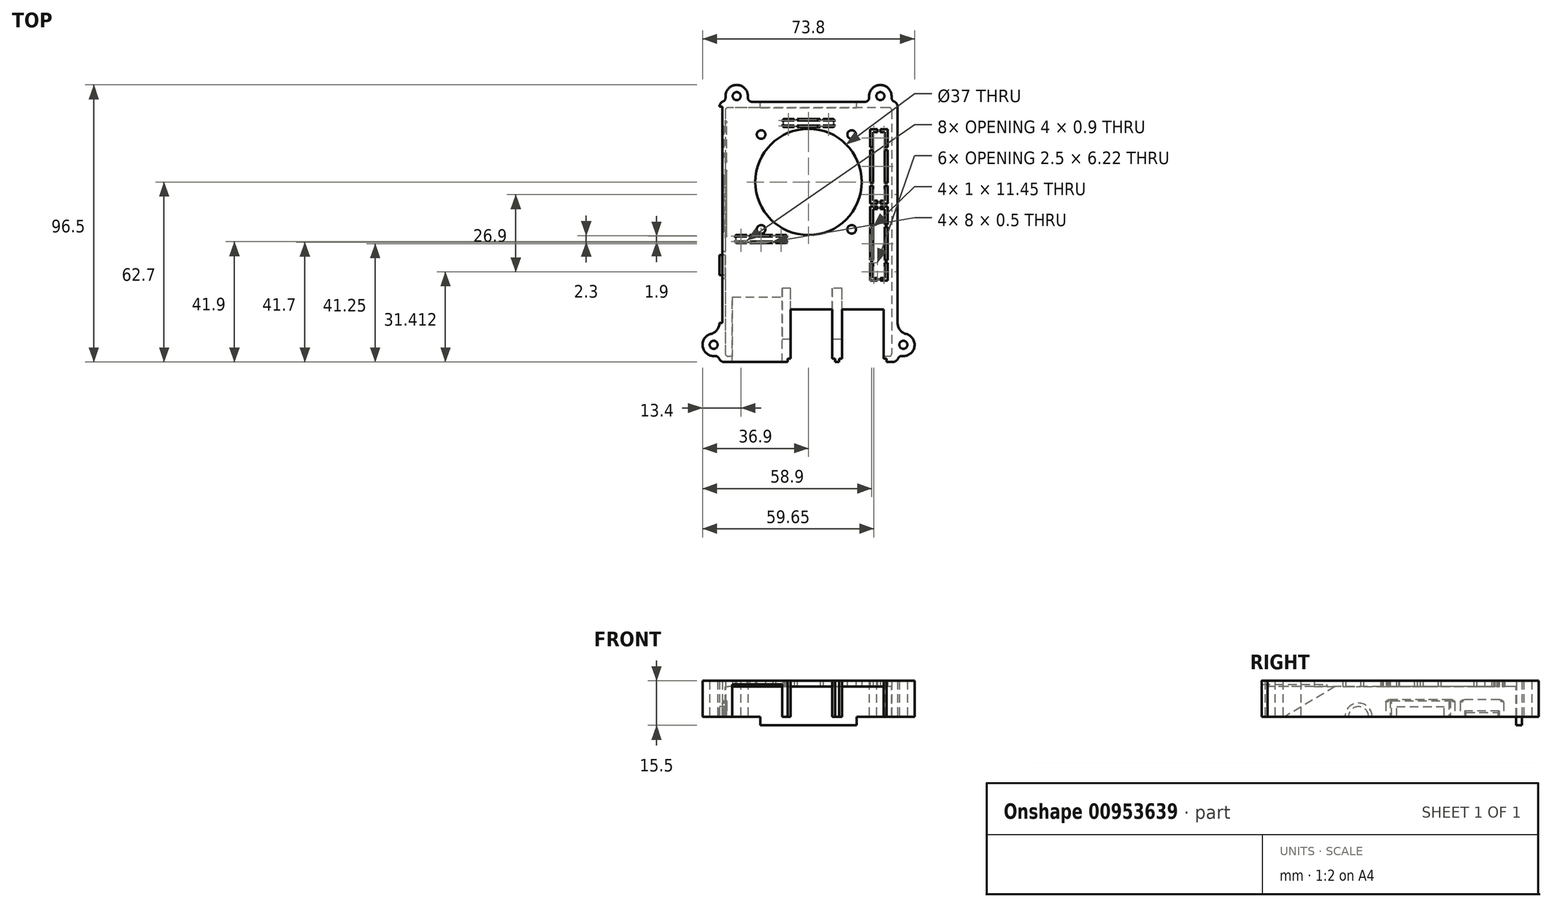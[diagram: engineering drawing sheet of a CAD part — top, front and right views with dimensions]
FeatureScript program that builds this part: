
annotation { "Feature Type Name" : "Feature", "Feature Type Description" : "" }
export const myFeature = defineFeature(function(context is Context, id is Id, definition is map)
    precondition{}
    {
        {
            var Q0;
            Q0=qCreatedBy(makeId("Top.planeOp"),FACE);
            var sketch = newSketch(context, id + "F0", { "sketchPlane" : qUnion([Q0])});
            skLineSegment(sketch, "E0.bottom", {"start": v(28, 43.3) * mm, "end": v(-28, 43.3) * mm});
            skLineSegment(sketch, "E0.top", {"start": v(28, -43.3) * mm, "end": v(-28, -43.3) * mm});
            skLineSegment(sketch, "E0.left", {"start": v(29, 42.3) * mm, "end": v(29, -42.3) * mm});
            skLineSegment(sketch, "E0.right", {"start": v(-29, 42.3) * mm, "end": v(-29, -42.3) * mm});
            skPoint(sketch, "E0.middle", {"position": v(0, 0) * mm});
            skLineSegment(sketch, "E1.0", {"start": v(31, 45.3) * mm, "end": v(31, -31.66) * mm});
            skLineSegment(sketch, "E1.1", {"start": v(31, 45.3) * mm, "end": v(30.38, 45.3) * mm});
            skLineSegment(sketch, "E1.2", {"start": v(-31, 45.3) * mm, "end": v(-31, -31.66) * mm});
            skLineSegment(sketch, "E1.3", {"start": v(31, -45.3) * mm, "end": v(-31, -45.3) * mm});
            skCircle(sketch, "E2", {"center": v(-25, 47.3) * mm, "radius": 1.4 * mm});
            skCircle(sketch, "E3", {"center": v(-33, -39.3) * mm, "radius": 1.4 * mm});
            skArc(sketch, "E4", {"start": v(-33.99, -35.53) * mm, "mid": v(-36.84, -39.98) * mm, "end": v(-32.64, -43.18) * mm});
            skArc(sketch, "E5", {"start": v(-21.12, 46.94) * mm, "mid": v(-25, 51.2) * mm, "end": v(-28.88, 46.94) * mm});
            skLineSegment(sketch, "E6.trimOffspring", {"start": v(-30.38, 45.3) * mm, "end": v(-31, 45.3) * mm});
            skLineSegment(sketch, "E7.trimOffspring", {"start": v(-31, -44.68) * mm, "end": v(-31, -45.3) * mm});
            skPoint(sketch, "E8.visualSharp", {"position": v(-31, -35.95) * mm});
            skArc(sketch, "E8.filletArc", {"start": v(-33.99, -35.53) * mm, "mid": v(-31.83, -34.1) * mm, "end": v(-31, -31.66) * mm});
            skPoint(sketch, "E9.visualSharp", {"position": v(-31, -42.65) * mm});
            skArc(sketch, "E9.filletArc", {"start": v(-31, -44.68) * mm, "mid": v(-31.49, -43.57) * mm, "end": v(-32.64, -43.18) * mm});
            skPoint(sketch, "E10.visualSharp", {"position": v(-28.35, 45.3) * mm});
            skArc(sketch, "E10.filletArc", {"start": v(-30.38, 45.3) * mm, "mid": v(-29.27, 45.79) * mm, "end": v(-28.88, 46.94) * mm});
            skPoint(sketch, "E11.visualSharp", {"position": v(-21.65, 45.3) * mm});
            skArc(sketch, "E11.filletArc", {"start": v(-21.12, 46.94) * mm, "mid": v(-20.73, 45.79) * mm, "end": v(-19.62, 45.3) * mm});
            skArc(sketch, "E12.MirrorCS", {"start": v(21.12, 46.94) * mm, "mid": v(20.73, 45.79) * mm, "end": v(19.62, 45.3) * mm});
            skCircle(sketch, "E13.MirrorC", {"center": v(25, 47.3) * mm, "radius": 1.4 * mm});
            skArc(sketch, "E14.MirrorCS", {"start": v(21.12, 46.94) * mm, "mid": v(25, 51.2) * mm, "end": v(28.88, 46.94) * mm});
            skArc(sketch, "E15.MirrorCS", {"start": v(30.38, 45.3) * mm, "mid": v(29.27, 45.79) * mm, "end": v(28.88, 46.94) * mm});
            skLineSegment(sketch, "E16.trimOffspring", {"start": v(19.62, 45.3) * mm, "end": v(-19.62, 45.3) * mm});
            skArc(sketch, "E17.MirrorCS", {"start": v(31, -44.68) * mm, "mid": v(31.49, -43.57) * mm, "end": v(32.64, -43.18) * mm});
            skCircle(sketch, "E18.MirrorC", {"center": v(33, -39.3) * mm, "radius": 1.4 * mm});
            skArc(sketch, "E19.MirrorCS", {"start": v(33.99, -35.53) * mm, "mid": v(36.84, -39.98) * mm, "end": v(32.64, -43.18) * mm});
            skArc(sketch, "E20.MirrorCS", {"start": v(33.99, -35.53) * mm, "mid": v(31.83, -34.1) * mm, "end": v(31, -31.66) * mm});
            skLineSegment(sketch, "E21.trimOffspring", {"start": v(31, -44.68) * mm, "end": v(31, -45.3) * mm});
            skPoint(sketch, "E22.visualSharp", {"position": v(-29, 43.3) * mm});
            skArc(sketch, "E22.filletArc", {"start": v(-28, 43.3) * mm, "mid": v(-28.7, 43) * mm, "end": v(-29, 42.3) * mm});
            skPoint(sketch, "E23.visualSharp", {"position": v(29, 43.3) * mm});
            skArc(sketch, "E23.filletArc", {"start": v(29, 42.3) * mm, "mid": v(28.7, 43) * mm, "end": v(28, 43.3) * mm});
            skPoint(sketch, "E24.visualSharp", {"position": v(-29, -43.3) * mm});
            skArc(sketch, "E24.filletArc", {"start": v(-29, -42.3) * mm, "mid": v(-28.7, -43) * mm, "end": v(-28, -43.3) * mm});
            skPoint(sketch, "E25.visualSharp", {"position": v(29, -43.3) * mm});
            skArc(sketch, "E25.filletArc", {"start": v(28, -43.3) * mm, "mid": v(28.7, -43) * mm, "end": v(29, -42.3) * mm});
            skLineSegment(sketch, "E26", {"start": v(-37.54, 31.4) * mm, "end": v(37.46, 31.4) * mm, "construction": true});
            skLineSegment(sketch, "E27", {"start": v(-37.54, 9.95) * mm, "end": v(37.46, 9.95) * mm, "construction": true});
            skLineSegment(sketch, "E28", {"start": v(-37.54, -11.55) * mm, "end": v(37.46, -11.55) * mm, "construction": true});
            skSolve(sketch);
        }
        {
            var Q0;
            Q0=makeQuery(id+"F0.imprint","IMPRINT",FACE,{"disambiguationData":[TD([[makeQuery(id+"F0.imprint","IMPRINT",EDGE,{"derivedFrom":sQuery(id+"F0.wireOp",EDGE,"E0.bottom")}),1.0]])]});
            var Q1;
            Q1=makeQuery(id+"F0.imprint","IMPRINT",FACE,{"disambiguationData":[TD([[makeQuery(id+"F0.imprint","IMPRINT",EDGE,{"derivedFrom":sQuery(id+"F0.wireOp",EDGE,"E0.bottom")}),-1.0]])]});
            var Q2;
            Q2=makeQuery(id+"F0.imprint","IMPRINT",FACE,{"disambiguationData":[TD([[makeQuery(id+"F0.imprint","IMPRINT",EDGE,{"derivedFrom":sQuery(id+"F0.wireOp",EDGE,"7KksbeZt-SgtM-qwzp-tZSZ-AhoeQB65ukFO")}),-1.0]])]});
            var Q3;
            Q3=makeQuery(id+"F0.imprint","IMPRINT",FACE,{"disambiguationData":[TD([[makeQuery(id+"F0.imprint","IMPRINT",EDGE,{"derivedFrom":sQuery(id+"F0.wireOp",EDGE,"7KksbeZt-SgtM-qwzp-tZSZ-AhoeQB65ukFO")}),1.0]])]});
            var Q4;
            Q4=makeQuery(id+"F0.imprint","IMPRINT",FACE,{"disambiguationData":[TD([[makeQuery(id+"F0.imprint","IMPRINT",EDGE,{"derivedFrom":sQuery(id+"F0.wireOp",EDGE,"5cbfba80-aa27-4a75-af92-75ae06634ded2.MirrorC")}),-1.0]])]});
            var Q5;
            Q5=makeQuery(id+"F0.imprint","IMPRINT",FACE,{"disambiguationData":[TD([[makeQuery(id+"F0.imprint","IMPRINT",EDGE,{"derivedFrom":sQuery(id+"F0.wireOp",EDGE,"5cbfba80-aa27-4a75-af92-75ae06634ded3.MirrorC")}),-1.0]])]});
            var Q6;
            Q6=makeQuery(id+"F0.imprint","IMPRINT",FACE,{"disambiguationData":[TD([[makeQuery(id+"F0.imprint","IMPRINT",EDGE,{"derivedFrom":sQuery(id+"F0.wireOp",EDGE,"8kVExDtM-LJhc-sOQH-PAKS-U9v5TH0pJNTE")}),-1.0]])]});
            var Q7;
            Q7=makeQuery(id+"F0.imprint","IMPRINT",FACE,{"disambiguationData":[TD([[makeQuery(id+"F0.imprint","IMPRINT",EDGE,{"derivedFrom":sQuery(id+"F0.wireOp",EDGE,"8kVExDtM-LJhc-sOQH-PAKS-U9v5TH0pJNTE")}),1.0]])]});
            var Q8;
            Q8=makeQuery(id+"F0.imprint","IMPRINT",FACE,{"disambiguationData":[TD([[makeQuery(id+"F0.imprint","IMPRINT",EDGE,{"derivedFrom":sQuery(id+"F0.wireOp",EDGE,"5cbfba80-aa27-4a75-af92-75ae06634ded0.MirrorC")}),-1.0]])]});
            var Q9;
            Q9=makeQuery(id+"F0.imprint","IMPRINT",FACE,{"disambiguationData":[TD([[makeQuery(id+"F0.imprint","IMPRINT",EDGE,{"derivedFrom":sQuery(id+"F0.wireOp",EDGE,"5cbfba80-aa27-4a75-af92-75ae06634ded0.MirrorC")}),1.0]])]});
            var Q10;
            Q10=makeQuery(id+"F0.imprint","IMPRINT",FACE,{"disambiguationData":[TD([[makeQuery(id+"F0.imprint","IMPRINT",EDGE,{"derivedFrom":sQuery(id+"F0.wireOp",EDGE,"dfaf72c4-a94b-42d6-8991-cf29f6b001300.MirrorC")}),-1.0]])]});
            var Q11;
            Q11=makeQuery(id+"F0.imprint","IMPRINT",FACE,{"disambiguationData":[TD([[makeQuery(id+"F0.imprint","IMPRINT",EDGE,{"derivedFrom":sQuery(id+"F0.wireOp",EDGE,"172ebd0b-a341-4e72-a369-0b862791728b.0")}),1.0]])]});
            var Q12;
            Q12=makeQuery(id+"F0.imprint","IMPRINT",FACE,{"disambiguationData":[TD([[makeQuery(id+"F0.imprint","IMPRINT",EDGE,{"derivedFrom":sQuery(id+"F0.wireOp",EDGE,"ufD7rTX0-MYzA-UZ21-AQa8-zzvgIyV9lOAw")}),1.0]])]});
            var Q13;
            Q13=makeQuery(id+"F0.imprint","IMPRINT",FACE,{"disambiguationData":[TD([[makeQuery(id+"F0.imprint","IMPRINT",EDGE,{"derivedFrom":sQuery(id+"F0.wireOp",EDGE,"5cbfba80-aa27-4a75-af92-75ae06634ded1.MirrorC")}),-1.0]])]});
            var Q14;
            Q14=makeQuery(id+"F0.imprint","IMPRINT",FACE,{"disambiguationData":[TD([[makeQuery(id+"F0.imprint","IMPRINT",EDGE,{"derivedFrom":sQuery(id+"F0.wireOp",EDGE,"56ec82e7-5166-41e1-9a52-937cd590b01a0.MirrorC")}),-1.0]])]});
            var Q15;
            Q15=makeQuery(id+"F0.imprint","IMPRINT",FACE,{"disambiguationData":[TD([[makeQuery(id+"F0.imprint","IMPRINT",EDGE,{"derivedFrom":sQuery(id+"F0.wireOp",EDGE,"b029ced5-7113-40fa-8cfa-9b4cbc9cc729.0")}),1.0]])]});
            var Q16;
            Q16=makeQuery(id+"F0.imprint","IMPRINT",FACE,{"disambiguationData":[TD([[makeQuery(id+"F0.imprint","IMPRINT",EDGE,{"derivedFrom":sQuery(id+"F0.wireOp",EDGE,"Lkb11Qj8-9LyP-TiyD-kAvs-BMHExQBuDsE0")}),1.0]])]});
            extrude(context, id + "F1", {"entities" : qUnion([Q0, Q1, Q2, Q3, Q4, Q5, Q6, Q7, Q8, Q9, Q10, Q11, Q12, Q13, Q14, Q15, Q16]), "depth" : 2 * mm, "offsetDistance" : 25 * mm});
        }
        {
            var Q0;
            Q0=makeQuery(id+"F0.imprint","IMPRINT",FACE,{"disambiguationData":[TD([[makeQuery(id+"F0.imprint","IMPRINT",EDGE,{"derivedFrom":sQuery(id+"F0.wireOp",EDGE,"E0.bottom")}),-1.0]])]});
            extrude(context, id + "F2", {"entities" : qUnion([Q0]), "operationType" : NewBodyOperationType.ADD, "oppositeDirection" : true, "depth" : 10.5 * mm, "offsetDistance" : 25 * mm});
        }
        {
            var Q0;
            {var subQ0=sQuery(id+"F0.wireOp",EDGE,"E6.trimOffspring");var subQ1=sQuery(id+"F0.wireOp",EDGE,"E1.2");Q0=makeQuery(id+"F2.boolean.opBoolean","MERGE",EDGE,{"derivedFrom":[makeQuery(id+"F1.opExtrude","SWEPT_EDGE",EDGE,{"disambiguationData":[OSD([subQ1,subQ0])]}),makeQuery(id+"F2.opExtrude","SWEPT_EDGE",EDGE,{"disambiguationData":[OSD([subQ1,subQ0])]})]});}
            var Q1;
            {var subQ0=sQuery(id+"F0.wireOp",EDGE,"E1.1");var subQ1=sQuery(id+"F0.wireOp",EDGE,"E1.0");Q1=makeQuery(id+"F2.boolean.opBoolean","MERGE",EDGE,{"derivedFrom":[makeQuery(id+"F1.opExtrude","SWEPT_EDGE",EDGE,{"disambiguationData":[OSD([subQ1,subQ0])]}),makeQuery(id+"F2.opExtrude","SWEPT_EDGE",EDGE,{"disambiguationData":[OSD([subQ1,subQ0])]})]});}
            var Q2;
            {var subQ0=sQuery(id+"F0.wireOp",EDGE,"E7.trimOffspring");var subQ1=sQuery(id+"F0.wireOp",EDGE,"E1.3");Q2=makeQuery(id+"F2.boolean.opBoolean","MERGE",EDGE,{"derivedFrom":[makeQuery(id+"F1.opExtrude","SWEPT_EDGE",EDGE,{"disambiguationData":[OSD([subQ1,subQ0])]}),makeQuery(id+"F2.opExtrude","SWEPT_EDGE",EDGE,{"disambiguationData":[OSD([subQ1,subQ0])]})]});}
            var Q3;
            {var subQ0=sQuery(id+"F0.wireOp",EDGE,"E21.trimOffspring");var subQ1=sQuery(id+"F0.wireOp",EDGE,"E1.3");Q3=makeQuery(id+"F2.boolean.opBoolean","MERGE",EDGE,{"derivedFrom":[makeQuery(id+"F1.opExtrude","SWEPT_EDGE",EDGE,{"disambiguationData":[OSD([subQ1,subQ0])]}),makeQuery(id+"F2.opExtrude","SWEPT_EDGE",EDGE,{"disambiguationData":[OSD([subQ1,subQ0])]})]});}
            fillet(context, id + "F3", {"entities" : qUnion([Q0, Q1, Q2, Q3]), "radius" : 2 * mm, "tangentPropagation" : true, "allowEdgeOverflow" : false});
        }
        {
            var Q0;
            Q0=makeQuery(id+"F2.opExtrude","CAP_FACE",FACE,{"disambiguationData":[OSD([sQuery(id+"F0.wireOp",EDGE,"E0.bottom"),sQuery(id+"F0.wireOp",EDGE,"E0.top"),sQuery(id+"F0.wireOp",EDGE,"E0.left"),sQuery(id+"F0.wireOp",EDGE,"E0.right"),sQuery(id+"F0.wireOp",EDGE,"E1.0"),sQuery(id+"F0.wireOp",EDGE,"E1.1"),sQuery(id+"F0.wireOp",EDGE,"E1.2"),sQuery(id+"F0.wireOp",EDGE,"E1.3"),sQuery(id+"F0.wireOp",EDGE,"E2"),sQuery(id+"F0.wireOp",EDGE,"E3"),sQuery(id+"F0.wireOp",EDGE,"E4"),sQuery(id+"F0.wireOp",EDGE,"E5"),sQuery(id+"F0.wireOp",EDGE,"E6.trimOffspring"),sQuery(id+"F0.wireOp",EDGE,"E7.trimOffspring"),sQuery(id+"F0.wireOp",EDGE,"E8.filletArc"),sQuery(id+"F0.wireOp",EDGE,"E9.filletArc"),sQuery(id+"F0.wireOp",EDGE,"E10.filletArc"),sQuery(id+"F0.wireOp",EDGE,"E11.filletArc"),sQuery(id+"F0.wireOp",EDGE,"E12.MirrorCS"),sQuery(id+"F0.wireOp",EDGE,"E13.MirrorC"),sQuery(id+"F0.wireOp",EDGE,"E14.MirrorCS"),sQuery(id+"F0.wireOp",EDGE,"E15.MirrorCS"),sQuery(id+"F0.wireOp",EDGE,"E16.trimOffspring"),sQuery(id+"F0.wireOp",EDGE,"E17.MirrorCS"),sQuery(id+"F0.wireOp",EDGE,"E18.MirrorC"),sQuery(id+"F0.wireOp",EDGE,"E19.MirrorCS"),sQuery(id+"F0.wireOp",EDGE,"E20.MirrorCS"),sQuery(id+"F0.wireOp",EDGE,"E21.trimOffspring"),sQuery(id+"F0.wireOp",EDGE,"E22.filletArc"),sQuery(id+"F0.wireOp",EDGE,"E23.filletArc"),sQuery(id+"F0.wireOp",EDGE,"E24.filletArc"),sQuery(id+"F0.wireOp",EDGE,"E25.filletArc")])],"isStart":false});
            var sketch = newSketch(context, id + "F4", { "sketchPlane" : qUnion([Q0])});
            skLineSegment(sketch, "E29.left", {"start": v(-29, -23.9) * mm, "end": v(-29, -38.9) * mm});
            skLineSegment(sketch, "E29.right", {"start": v(-28.5, -24.4) * mm, "end": v(-28.5, -38.4) * mm});
            skLineSegment(sketch, "E30", {"start": v(-29, -23.9) * mm, "end": v(-28.5, -24.4) * mm});
            skLineSegment(sketch, "E31", {"start": v(-29, -38.9) * mm, "end": v(-28.5, -38.4) * mm});
            skLineSegment(sketch, "E32.left", {"start": v(-29, 2.05) * mm, "end": v(-29, -21.95) * mm});
            skLineSegment(sketch, "E32.right", {"start": v(-28.5, 1.55) * mm, "end": v(-28.5, -21.45) * mm});
            skLineSegment(sketch, "E33", {"start": v(-29, 2.05) * mm, "end": v(-28.5, 1.55) * mm});
            skLineSegment(sketch, "E34", {"start": v(-29, -21.95) * mm, "end": v(-28.5, -21.45) * mm});
            skSolve(sketch);
        }
        {
            var Q0;
            Q0=qSketchRegion(id+"F4",true);
            extrude(context, id + "F5", {"entities" : qUnion([Q0]), "operationType" : NewBodyOperationType.ADD, "oppositeDirection" : true, "depth" : 6 * mm, "offsetDistance" : 25 * mm});
        }
        {
            var Q0;
            Q0=makeQuery(id+"F5.opExtrude","CAP_EDGE",EDGE,{"disambiguationData":[OSD([sQuery(id+"F4.wireOp",EDGE,"E32.right")])],"isStart":false});
            var Q1;
            Q1=makeQuery(id+"F5.opExtrude","CAP_EDGE",EDGE,{"disambiguationData":[OSD([sQuery(id+"F4.wireOp",EDGE,"E29.right")])],"isStart":false});
            var Q2;
            Q2=makeQuery(id+"F5.opExtrude","CAP_EDGE",EDGE,{"disambiguationData":[OSD([sQuery(id+"F4.wireOp",EDGE,"E34")])],"isStart":false});
            var Q3;
            Q3=makeQuery(id+"F5.opExtrude","CAP_EDGE",EDGE,{"disambiguationData":[OSD([sQuery(id+"F4.wireOp",EDGE,"E33")])],"isStart":false});
            var Q4;
            Q4=makeQuery(id+"F5.opExtrude","CAP_EDGE",EDGE,{"disambiguationData":[OSD([sQuery(id+"F4.wireOp",EDGE,"E31")])],"isStart":false});
            var Q5;
            Q5=makeQuery(id+"F5.opExtrude","CAP_EDGE",EDGE,{"disambiguationData":[OSD([sQuery(id+"F4.wireOp",EDGE,"E30")])],"isStart":false});
            fillet(context, id + "F6", {"entities" : qUnion([Q0, Q1, Q2, Q3, Q4, Q5]), "radius" : 1 * mm, "tangentPropagation" : true, "allowEdgeOverflow" : false});
        }
        {
            var Q0;
            Q0=makeQuery(id+"F6.opFillet","BLEND_EDGE",EDGE,{"blendedFrom":[makeQuery(id+"F5.opExtrude","CAP_EDGE",EDGE,{"disambiguationData":[OSD([sQuery(id+"F4.wireOp",EDGE,"E32.right")])],"isStart":false}),makeQuery(id+"F5.opExtrude","CAP_EDGE",EDGE,{"disambiguationData":[OSD([sQuery(id+"F4.wireOp",EDGE,"E34")])],"isStart":false})],"blendedInto":[]});
            var Q1;
            Q1=makeQuery(id+"F6.opFillet","BLEND_EDGE",EDGE,{"blendedFrom":[makeQuery(id+"F5.opExtrude","CAP_EDGE",EDGE,{"disambiguationData":[OSD([sQuery(id+"F4.wireOp",EDGE,"E32.right")])],"isStart":false}),makeQuery(id+"F5.opExtrude","CAP_EDGE",EDGE,{"disambiguationData":[OSD([sQuery(id+"F4.wireOp",EDGE,"E33")])],"isStart":false})],"blendedInto":[]});
            var Q2;
            Q2=makeQuery(id+"F6.opFillet","BLEND_EDGE",EDGE,{"blendedFrom":[makeQuery(id+"F5.opExtrude","CAP_EDGE",EDGE,{"disambiguationData":[OSD([sQuery(id+"F4.wireOp",EDGE,"E29.right")])],"isStart":false}),makeQuery(id+"F5.opExtrude","CAP_EDGE",EDGE,{"disambiguationData":[OSD([sQuery(id+"F4.wireOp",EDGE,"E31")])],"isStart":false})],"blendedInto":[]});
            var Q3;
            Q3=makeQuery(id+"F5.opExtrude","SWEPT_EDGE",EDGE,{"disambiguationData":[OSD([sQuery(id+"F4.wireOp",EDGE,"E29.right"),sQuery(id+"F4.wireOp",EDGE,"E30")])]});
            fillet(context, id + "F7", {"entities" : qUnion([Q0, Q1, Q2, Q3]), "radius" : 0.5 * mm, "tangentPropagation" : true, "allowEdgeOverflow" : false});
        }
        {
            var Q0;
            Q0=qCreatedBy(makeId("Right.planeOp"),FACE);
            var sketch = newSketch(context, id + "F8", { "sketchPlane" : qUnion([Q0])});
            skLineSegment(sketch, "E35", {"start": v(31.4, -3.36) * mm, "end": v(31.4, 15) * mm, "construction": true});
            skLineSegment(sketch, "E36", {"start": v(9.95, -3.36) * mm, "end": v(9.95, 15) * mm, "construction": true});
            skLineSegment(sketch, "E37", {"start": v(-11.55, -3.36) * mm, "end": v(-11.55, 15) * mm, "construction": true});
            skSolve(sketch);
        }
        {
            var Q0;
            {var subQ0=sQuery(id+"F0.wireOp",EDGE,"E1.2");Q0=makeQuery(id+"F2.boolean.opBoolean","MERGE",FACE,{"derivedFrom":[makeQuery(id+"F1.opExtrude","SWEPT_FACE",FACE,{"disambiguationData":[OSD([subQ0])]}),makeQuery(id+"F2.opExtrude","SWEPT_FACE",FACE,{"disambiguationData":[OSD([subQ0])]})]});}
            var sketch = newSketch(context, id + "F9", { "sketchPlane" : qUnion([Q0])});
            skArc(sketch, "E38.MirrorCS", {"start": v(6.8, -10.5) * mm, "mid": v(11.55, -5.75) * mm, "end": v(16.3, -10.5) * mm});
            skArc(sketch, "E39.MirrorCS", {"start": v(8.05, -10.5) * mm, "mid": v(11.55, -7) * mm, "end": v(15.05, -10.5) * mm});
            skPoint(sketch, "E40.end.orphan", {"position": v(15.05, -10.5) * mm});
            skPoint(sketch, "E40.start.orphan", {"position": v(8.05, -10.5) * mm});
            skPoint(sketch, "E41.end.orphan", {"position": v(16.3, -10.5) * mm});
            skPoint(sketch, "E41.start.orphan", {"position": v(6.8, -10.5) * mm});
            skSolve(sketch);
        }
        {
            var Q0;
            {var subQ0=sQuery(id+"F9.wireOp",EDGE,"E39.MirrorCS");Q0=makeQuery(id+"F9.imprint","IMPRINT",FACE,{"disambiguationData":[TD([[makeQuery(id+"F9.imprint","IMPRINT",EDGE,{"derivedFrom":subQ0}),-1.0]])]});}
            var Q1;
            Q1=makeQuery(id+"F2.opExtrude","SWEPT_FACE",FACE,{"disambiguationData":[OSD([sQuery(id+"F0.wireOp",EDGE,"E0.right")])]});
            extrude(context, id + "F10", {"entities" : qUnion([Q0]), "operationType" : NewBodyOperationType.REMOVE, "endBound" : BoundingType.UP_TO_SURFACE, "oppositeDirection" : true, "depth" : 25 * mm, "endBoundEntityFace" : qUnion([Q1]), "offsetDistance" : 25 * mm});
        }
        {
            var Q0;
            {var subQ0=sQuery(id+"F9.wireOp",EDGE,"E38.MirrorCS");Q0=makeQuery(id+"F9.imprint","IMPRINT",FACE,{"disambiguationData":[TD([[makeQuery(id+"F9.imprint","IMPRINT",EDGE,{"derivedFrom":subQ0}),-1.0]])]});}
            extrude(context, id + "F11", {"entities" : qUnion([Q0]), "operationType" : NewBodyOperationType.REMOVE, "oppositeDirection" : true, "depth" : 1 * mm, "offsetDistance" : 25 * mm});
        }
        {
            var Q0;
            {var subQ5=sQuery(id+"F9.wireOp",EDGE,"E38.MirrorCS");Q0=makeQuery(id+"F9.imprint","IMPRINT",FACE,{"disambiguationData":[TD([[makeQuery(id+"F9.imprint","IMPRINT",EDGE,{"derivedFrom":subQ5}),1.0]])]});}
            var sketch = newSketch(context, id + "F12", { "sketchPlane" : qUnion([Q0])});
            skLineSegment(sketch, "E42.bottom", {"start": v(-20.45, -4.5) * mm, "end": v(0.55, -4.5) * mm});
            skLineSegment(sketch, "E42.top", {"start": v(-20.45, -10.5) * mm, "end": v(0.55, -10.5) * mm});
            skLineSegment(sketch, "E42.left", {"start": v(-20.45, -4.5) * mm, "end": v(-20.45, -10.5) * mm});
            skLineSegment(sketch, "E42.right", {"start": v(0.55, -4.5) * mm, "end": v(0.55, -10.5) * mm});
            skLineSegment(sketch, "E43.0", {"start": v(-18.2, -7) * mm, "end": v(-18.2, -10.5) * mm});
            skLineSegment(sketch, "E44.0", {"start": v(-1.7, -7) * mm, "end": v(-1.7, -10.5) * mm});
            skLineSegment(sketch, "E45.0", {"start": v(-18.2, -7) * mm, "end": v(-1.7, -7) * mm});
            skLineSegment(sketch, "E46.bottom", {"start": v(-37.4, -8.5) * mm, "end": v(-25.4, -8.5) * mm});
            skLineSegment(sketch, "E46.top", {"start": v(-37.4, -10.5) * mm, "end": v(-25.4, -10.5) * mm});
            skLineSegment(sketch, "E46.left", {"start": v(-37.4, -8.5) * mm, "end": v(-37.4, -10.5) * mm});
            skLineSegment(sketch, "E46.right", {"start": v(-25.4, -8.5) * mm, "end": v(-25.4, -10.5) * mm});
            skSolve(sketch);
        }
        {
            var Q0;
            Q0=makeQuery(id+"F12.imprint","IMPRINT",FACE,{"disambiguationData":[TD([[makeQuery(id+"F12.imprint","IMPRINT",EDGE,{"derivedFrom":sQuery(id+"F12.wireOp",EDGE,"E46.bottom")}),-1.0]])]});
            var Q1;
            {var subQ0=sQuery(id+"F12.wireOp",EDGE,"2f087f3d-fe2a-414c-9c26-de2792726961.0");Q1=makeQuery(id+"F12.imprint","IMPRINT",FACE,{"disambiguationData":[TD([[makeQuery(id+"F12.imprint","IMPRINT",EDGE,{"derivedFrom":subQ0}),1.0]])]});}
            var Q2;
            Q2=makeQuery(id+"F12.imprint","IMPRINT",FACE,{"disambiguationData":[TD([[makeQuery(id+"F12.imprint","IMPRINT",EDGE,{"derivedFrom":sQuery(id+"F12.wireOp",EDGE,"E42.bottom")}),-1.0]])]});
            var Q3;
            {var subQ0=sQuery(id+"F12.wireOp",EDGE,"E43.0");Q3=makeQuery(id+"F12.imprint","IMPRINT",FACE,{"disambiguationData":[TD([[makeQuery(id+"F12.imprint","IMPRINT",EDGE,{"derivedFrom":subQ0}),1.0]])]});}
            var Q4;
            Q4=makeQuery(id+"F5.opExtrude","SWEPT_FACE",FACE,{"disambiguationData":[OSD([sQuery(id+"F4.wireOp",EDGE,"E29.right")])]});
            extrude(context, id + "F13", {"entities" : qUnion([Q0, Q1, Q2, Q3]), "operationType" : NewBodyOperationType.REMOVE, "oppositeDirection" : true, "depth" : 1.5 * mm, "endBoundEntityFace" : qUnion([Q4]), "offsetDistance" : 25 * mm});
        }
        {
            var Q0;
            {var subQ0=sQuery(id+"F12.wireOp",EDGE,"E43.0");Q0=makeQuery(id+"F12.imprint","IMPRINT",FACE,{"disambiguationData":[TD([[makeQuery(id+"F12.imprint","IMPRINT",EDGE,{"derivedFrom":subQ0}),1.0]])]});}
            var Q1;
            Q1=makeQuery(id+"F5.opExtrude","SWEPT_FACE",FACE,{"disambiguationData":[OSD([sQuery(id+"F4.wireOp",EDGE,"E29.right")])]});
            extrude(context, id + "F14", {"entities" : qUnion([Q0]), "operationType" : NewBodyOperationType.REMOVE, "endBound" : BoundingType.UP_TO_SURFACE, "oppositeDirection" : true, "depth" : 25 * mm, "endBoundEntityFace" : qUnion([Q1]), "offsetDistance" : 25 * mm});
        }
        {
            var Q0;
            Q0=makeQuery(id+"F13.boolean.opBoolean","COPY",EDGE,{"derivedFrom":makeQuery(id+"F13.opExtrude","CAP_EDGE",EDGE,{"disambiguationData":[OSD([sQuery(id+"F12.wireOp",EDGE,"E42.left")])],"isStart":false})});
            var Q1;
            Q1=makeQuery(id+"F13.boolean.opBoolean","COPY",EDGE,{"derivedFrom":makeQuery(id+"F13.opExtrude","CAP_EDGE",EDGE,{"disambiguationData":[OSD([sQuery(id+"F12.wireOp",EDGE,"E42.bottom")])],"isStart":false})});
            var Q2;
            Q2=makeQuery(id+"F13.boolean.opBoolean","COPY",EDGE,{"derivedFrom":makeQuery(id+"F13.opExtrude","CAP_EDGE",EDGE,{"disambiguationData":[OSD([sQuery(id+"F12.wireOp",EDGE,"E42.right")])],"isStart":false})});
            var Q3;
            Q3=makeQuery(id+"F13.boolean.opBoolean","COPY",EDGE,{"derivedFrom":makeQuery(id+"F13.opExtrude","CAP_EDGE",EDGE,{"disambiguationData":[OSD([sQuery(id+"F12.wireOp",EDGE,"E46.right")])],"isStart":false})});
            var Q4;
            Q4=makeQuery(id+"F13.boolean.opBoolean","COPY",EDGE,{"derivedFrom":makeQuery(id+"F13.opExtrude","CAP_EDGE",EDGE,{"disambiguationData":[OSD([sQuery(id+"F12.wireOp",EDGE,"E46.bottom")])],"isStart":false})});
            var Q5;
            Q5=makeQuery(id+"F13.boolean.opBoolean","COPY",EDGE,{"derivedFrom":makeQuery(id+"F13.opExtrude","CAP_EDGE",EDGE,{"disambiguationData":[OSD([sQuery(id+"F12.wireOp",EDGE,"E46.left")])],"isStart":false})});
            chamfer(context, id + "F15", {"entities" : qUnion([Q0, Q1, Q2, Q3, Q4, Q5]), "width" : 0.5 * mm, "tangentPropagation" : true});
        }
        {
            var Q0;
            {var subQ4=sQuery(id+"F0.wireOp",EDGE,"E16.trimOffspring");var subQ7=sQuery(id+"F0.wireOp",EDGE,"E12.MirrorCS");Q0=makeQuery(id+"FgmCDMeV1RtUn8Z_1.boolean.opBoolean","SPLIT",FACE,{"disambiguationData":[TD([makeQuery(id+"F1.opExtrude","SWEPT_FACE",FACE,{"disambiguationData":[OSD([subQ7])]})])],"derivedFrom":makeQuery(id+"F2.boolean.opBoolean","MERGE",FACE,{"derivedFrom":[makeQuery(id+"F1.opExtrude","SWEPT_FACE",FACE,{"disambiguationData":[OSD([subQ4])]}),makeQuery(id+"F2.opExtrude","SWEPT_FACE",FACE,{"disambiguationData":[OSD([subQ4])]})]})});}
            var sketch = newSketch(context, id + "F16", { "sketchPlane" : qUnion([Q0])});
            skLineSegment(sketch, "E47.bottom", {"start": v(-16.8, -10.5) * mm, "end": v(16.8, -10.5) * mm});
            skLineSegment(sketch, "E47.top", {"start": v(-16.8, -13.5) * mm, "end": v(16.8, -13.5) * mm});
            skLineSegment(sketch, "E47.left", {"start": v(-16.8, -10.5) * mm, "end": v(-16.8, -13.5) * mm});
            skLineSegment(sketch, "E47.right", {"start": v(16.8, -10.5) * mm, "end": v(16.8, -13.5) * mm});
            skSolve(sketch);
        }
        {
            var Q0;
            Q0=makeQuery(id+"F16.imprint","IMPRINT",FACE,{"disambiguationData":[TD([[makeQuery(id+"F16.imprint","IMPRINT",EDGE,{"derivedFrom":sQuery(id+"F16.wireOp",EDGE,"E47.bottom")}),-1.0]])]});
            var Q1;
            Q1=makeQuery(id+"F2.opExtrude","SWEPT_FACE",FACE,{"disambiguationData":[OSD([sQuery(id+"F0.wireOp",EDGE,"E0.bottom")])]});
            extrude(context, id + "F17", {"entities" : qUnion([Q0]), "operationType" : NewBodyOperationType.ADD, "endBound" : BoundingType.UP_TO_SURFACE, "oppositeDirection" : true, "depth" : 2 * mm, "endBoundEntityFace" : qUnion([Q1]), "offsetDistance" : 25 * mm});
        }
        {
            var Q0;
            {var subQ0=sQuery(id+"F0.wireOp",EDGE,"E4");var subQ2=sQuery(id+"F0.wireOp",EDGE,"E0.left");var subQ4=sQuery(id+"F0.wireOp",EDGE,"E0.top");var subQ6=sQuery(id+"F0.wireOp",EDGE,"E1.1");var subQ7=sQuery(id+"F0.wireOp",EDGE,"E1.0");var subQ9=sQuery(id+"F0.wireOp",EDGE,"E0.bottom");var subQ11=sQuery(id+"F0.wireOp",EDGE,"E3");var subQ13=sQuery(id+"F0.wireOp",EDGE,"E20.MirrorCS");var subQ15=sQuery(id+"F0.wireOp",EDGE,"E19.MirrorCS");var subQ17=sQuery(id+"F0.wireOp",EDGE,"E1.3");var subQ19=sQuery(id+"F0.wireOp",EDGE,"E17.MirrorCS");var subQ25=sQuery(id+"F0.wireOp",EDGE,"E1.2");var subQ27=sQuery(id+"F0.wireOp",EDGE,"E16.trimOffspring");var subQ30=sQuery(id+"F0.wireOp",EDGE,"E18.MirrorC");var subQ33=sQuery(id+"F0.wireOp",EDGE,"E7.trimOffspring");var subQ35=sQuery(id+"F0.wireOp",EDGE,"E14.MirrorCS");var subQ41=sQuery(id+"F0.wireOp",EDGE,"E15.MirrorCS");var subQ43=makeQuery(id+"F1.opExtrude","SWEPT_FACE",FACE,{"disambiguationData":[OSD([subQ7])]});var subQ45=sQuery(id+"F0.wireOp",EDGE,"E9.filletArc");var subQ47=sQuery(id+"F0.wireOp",EDGE,"E25.filletArc");var subQ49=sQuery(id+"F0.wireOp",EDGE,"E8.filletArc");var subQ51=sQuery(id+"F0.wireOp",EDGE,"E24.filletArc");var subQ53=sQuery(id+"F0.wireOp",EDGE,"E0.right");var subQ55=sQuery(id+"F0.wireOp",EDGE,"E21.trimOffspring");var subQ57=sQuery(id+"F0.wireOp",EDGE,"E12.MirrorCS");var subQ62=sQuery(id+"F0.wireOp",EDGE,"E13.MirrorC");var subQ68=sQuery(id+"F0.wireOp",EDGE,"E23.filletArc");var subQ70=sQuery(id+"F0.wireOp",EDGE,"E22.filletArc");var subQ71=sQuery(id+"F0.wireOp",EDGE,"E11.filletArc");var subQ72=sQuery(id+"F0.wireOp",EDGE,"E10.filletArc");var subQ73=sQuery(id+"F0.wireOp",EDGE,"E5");var subQ74=sQuery(id+"F0.wireOp",EDGE,"E6.trimOffspring");var subQ75=sQuery(id+"F0.wireOp",EDGE,"E2");var subQ76=sQuery(id+"F4.wireOp",EDGE,"E29.right");var subQ77=sQuery(id+"F4.wireOp",EDGE,"E30");Q0=makeQuery(id+"FgmCDMeV1RtUn8Z_1.boolean.opBoolean","SPLIT",FACE,{"disambiguationData":[TD([subQ43])],"derivedFrom":makeQuery(id+"F14.boolean.opBoolean","SPLIT",FACE,{"disambiguationData":[TD([subQ43])],"derivedFrom":makeQuery(id+"F5.boolean.opBoolean","MERGE",FACE,{"derivedFrom":[makeQuery(id+"F2.opExtrude","CAP_FACE",FACE,{"disambiguationData":[OSD([subQ9,subQ4,subQ2,subQ53,subQ7,subQ6,subQ25,subQ17,subQ75,subQ11,subQ0,subQ73,subQ74,subQ33,subQ49,subQ45,subQ72,subQ71,subQ57,subQ62,subQ35,subQ41,subQ27,subQ19,subQ30,subQ15,subQ13,subQ55,subQ70,subQ68,subQ51,subQ47])],"isStart":false}),makeQuery(id+"F5.opExtrude","CAP_FACE",FACE,{"disambiguationData":[OSD([sQuery(id+"F4.wireOp",EDGE,"E29.left"),subQ76,subQ77,sQuery(id+"F4.wireOp",EDGE,"E31")])],"isStart":true}),makeQuery(id+"F5.opExtrude","CAP_FACE",FACE,{"disambiguationData":[OSD([sQuery(id+"F4.wireOp",EDGE,"E32.left"),sQuery(id+"F4.wireOp",EDGE,"E32.right"),sQuery(id+"F4.wireOp",EDGE,"E33"),sQuery(id+"F4.wireOp",EDGE,"E34")])],"isStart":true})]})})});}
            var sketch = newSketch(context, id + "F18", { "sketchPlane" : qUnion([Q0])});
            skLineSegment(sketch, "E48", {"start": v(-7.7, 63.26) * mm, "end": v(-7.7, 18.26) * mm, "construction": true});
            skLineSegment(sketch, "E49", {"start": v(9.95, 63.26) * mm, "end": v(9.95, 18.26) * mm, "construction": true});
            skLineSegment(sketch, "E50.bottom", {"start": v(-9.1, 43.3) * mm, "end": v(-6.3, 43.3) * mm});
            skLineSegment(sketch, "E50.top", {"start": v(-9.1, 16.3) * mm, "end": v(-6.3, 16.3) * mm});
            skLineSegment(sketch, "E50.left", {"start": v(-9.1, 43.3) * mm, "end": v(-9.1, 16.3) * mm});
            skLineSegment(sketch, "E50.right", {"start": v(-6.3, 43.3) * mm, "end": v(-6.3, 16.3) * mm});
            skLineSegment(sketch, "E51.bottom", {"start": v(8.2, 43.3) * mm, "end": v(11.7, 43.3) * mm});
            skLineSegment(sketch, "E51.top", {"start": v(8.2, 16.3) * mm, "end": v(11.7, 16.3) * mm});
            skLineSegment(sketch, "E51.left", {"start": v(8.2, 43.3) * mm, "end": v(8.2, 16.3) * mm});
            skLineSegment(sketch, "E51.right", {"start": v(11.7, 43.3) * mm, "end": v(11.7, 16.3) * mm});
            skSolve(sketch);
        }
        {
            var Q0;
            Q0=qSketchRegion(id+"F18",true);
            var Q1;
            Q1=makeQuery(id+"F1.opExtrude","CAP_FACE",FACE,{"disambiguationData":[OSD([sQuery(id+"F0.wireOp",EDGE,"E1.0"),sQuery(id+"F0.wireOp",EDGE,"E1.1"),sQuery(id+"F0.wireOp",EDGE,"E1.2"),sQuery(id+"F0.wireOp",EDGE,"E1.3"),sQuery(id+"F0.wireOp",EDGE,"E2"),sQuery(id+"F0.wireOp",EDGE,"E3"),sQuery(id+"F0.wireOp",EDGE,"E4"),sQuery(id+"F0.wireOp",EDGE,"E5"),sQuery(id+"F0.wireOp",EDGE,"E6.trimOffspring"),sQuery(id+"F0.wireOp",EDGE,"E7.trimOffspring"),sQuery(id+"F0.wireOp",EDGE,"E8.filletArc"),sQuery(id+"F0.wireOp",EDGE,"E9.filletArc"),sQuery(id+"F0.wireOp",EDGE,"E10.filletArc"),sQuery(id+"F0.wireOp",EDGE,"E11.filletArc"),sQuery(id+"F0.wireOp",EDGE,"E12.MirrorCS"),sQuery(id+"F0.wireOp",EDGE,"E13.MirrorC"),sQuery(id+"F0.wireOp",EDGE,"E14.MirrorCS"),sQuery(id+"F0.wireOp",EDGE,"E15.MirrorCS"),sQuery(id+"F0.wireOp",EDGE,"E16.trimOffspring"),sQuery(id+"F0.wireOp",EDGE,"E17.MirrorCS"),sQuery(id+"F0.wireOp",EDGE,"E18.MirrorC"),sQuery(id+"F0.wireOp",EDGE,"E19.MirrorCS"),sQuery(id+"F0.wireOp",EDGE,"E20.MirrorCS"),sQuery(id+"F0.wireOp",EDGE,"E21.trimOffspring")])],"isStart":true});
            extrude(context, id + "F19", {"entities" : qUnion([Q0]), "operationType" : NewBodyOperationType.ADD, "endBound" : BoundingType.UP_TO_SURFACE, "oppositeDirection" : true, "depth" : 0.5 * mm, "endBoundEntityFace" : qUnion([Q1]), "offsetDistance" : 25 * mm});
        }
        {
            var Q0;
            Q0=makeQuery(id+"F19.opExtrude","CAP_EDGE",EDGE,{"disambiguationData":[OSD([sQuery(id+"F18.wireOp",EDGE,"E50.top")])],"isStart":true});
            var Q1;
            Q1=makeQuery(id+"F19.opExtrude","CAP_EDGE",EDGE,{"disambiguationData":[OSD([sQuery(id+"F18.wireOp",EDGE,"E51.top")])],"isStart":true});
            chamfer(context, id + "F20", {"entities" : qUnion([Q0, Q1]), "chamferType" : ChamferType.TWO_OFFSETS, "width1" : 21 * mm, "oppositeDirection" : false, "width2" : 12.5 * mm, "tangentPropagation" : true});
        }
        {
            var Q0;
            Q0=qCreatedBy(makeId("Top.planeOp"),FACE);
            var sketch = newSketch(context, id + "F21", { "sketchPlane" : qUnion([Q0])});
            skLineSegment(sketch, "E52", {"start": v(-17.75, 15.2) * mm, "end": v(-17.75, -55.38) * mm, "construction": true});
            skLineSegment(sketch, "E53", {"start": v(0.95, 15.2) * mm, "end": v(0.95, -55.38) * mm, "construction": true});
            skLineSegment(sketch, "E54", {"start": v(18.95, 15.2) * mm, "end": v(18.95, -55.38) * mm, "construction": true});
            skSolve(sketch);
        }
        {
            var Q0;
            Q0=makeQuery(id+"F1.opExtrude","CAP_FACE",FACE,{"disambiguationData":[OSD([sQuery(id+"F0.wireOp",EDGE,"E1.0"),sQuery(id+"F0.wireOp",EDGE,"E1.1"),sQuery(id+"F0.wireOp",EDGE,"E1.2"),sQuery(id+"F0.wireOp",EDGE,"E1.3"),sQuery(id+"F0.wireOp",EDGE,"E2"),sQuery(id+"F0.wireOp",EDGE,"E3"),sQuery(id+"F0.wireOp",EDGE,"E4"),sQuery(id+"F0.wireOp",EDGE,"E5"),sQuery(id+"F0.wireOp",EDGE,"E6.trimOffspring"),sQuery(id+"F0.wireOp",EDGE,"E7.trimOffspring"),sQuery(id+"F0.wireOp",EDGE,"E8.filletArc"),sQuery(id+"F0.wireOp",EDGE,"E9.filletArc"),sQuery(id+"F0.wireOp",EDGE,"E10.filletArc"),sQuery(id+"F0.wireOp",EDGE,"E11.filletArc"),sQuery(id+"F0.wireOp",EDGE,"E12.MirrorCS"),sQuery(id+"F0.wireOp",EDGE,"E13.MirrorC"),sQuery(id+"F0.wireOp",EDGE,"E14.MirrorCS"),sQuery(id+"F0.wireOp",EDGE,"E15.MirrorCS"),sQuery(id+"F0.wireOp",EDGE,"E16.trimOffspring"),sQuery(id+"F0.wireOp",EDGE,"E17.MirrorCS"),sQuery(id+"F0.wireOp",EDGE,"E18.MirrorC"),sQuery(id+"F0.wireOp",EDGE,"E19.MirrorCS"),sQuery(id+"F0.wireOp",EDGE,"E20.MirrorCS"),sQuery(id+"F0.wireOp",EDGE,"E21.trimOffspring")])],"isStart":true});
            var sketch = newSketch(context, id + "F22", { "sketchPlane" : qUnion([Q0])});
            skLineSegment(sketch, "E55.bottom", {"start": v(-9.1, 45.3) * mm, "end": v(-26.5, 45.3) * mm});
            skLineSegment(sketch, "E55.top", {"start": v(-9.1, 22.6) * mm, "end": v(-26.5, 22.6) * mm});
            skLineSegment(sketch, "E55.left", {"start": v(-9.1, 45.3) * mm, "end": v(-9.1, 22.6) * mm});
            skLineSegment(sketch, "E55.right", {"start": v(-26.5, 45.3) * mm, "end": v(-26.5, 22.6) * mm});
            skLineSegment(sketch, "E56.top", {"start": v(8.2, 27) * mm, "end": v(-6.3, 27) * mm});
            skLineSegment(sketch, "E56.left", {"start": v(8.2, 44.1) * mm, "end": v(8.2, 27) * mm});
            skLineSegment(sketch, "E56.right", {"start": v(-6.3, 44.1) * mm, "end": v(-6.3, 27) * mm});
            skLineSegment(sketch, "E57", {"start": v(-7.3, 44.1) * mm, "end": v(-6.3, 44.1) * mm});
            skLineSegment(sketch, "E58", {"start": v(9.2, 45.3) * mm, "end": v(9.2, 44.1) * mm});
            skLineSegment(sketch, "E59", {"start": v(9.2, 44.1) * mm, "end": v(8.2, 44.1) * mm});
            skLineSegment(sketch, "E60", {"start": v(-7.3, 45.3) * mm, "end": v(9.2, 45.3) * mm});
            skLineSegment(sketch, "E61", {"start": v(-7.3, 44.1) * mm, "end": v(-7.3, 45.3) * mm});
            skLineSegment(sketch, "E62.bottom", {"start": v(10.7, 45.3) * mm, "end": v(27.2, 45.3) * mm});
            skLineSegment(sketch, "E62.top", {"start": v(11.7, 27) * mm, "end": v(26.2, 27) * mm});
            skLineSegment(sketch, "E62.left", {"start": v(11.7, 44.1) * mm, "end": v(11.7, 27) * mm});
            skLineSegment(sketch, "E62.right", {"start": v(26.2, 44.1) * mm, "end": v(26.2, 27) * mm});
            skLineSegment(sketch, "E63", {"start": v(10.7, 45.3) * mm, "end": v(10.7, 44.1) * mm});
            skLineSegment(sketch, "E64", {"start": v(10.7, 44.1) * mm, "end": v(11.7, 44.1) * mm});
            skLineSegment(sketch, "E65", {"start": v(27.2, 45.3) * mm, "end": v(27.2, 44.1) * mm});
            skLineSegment(sketch, "E66", {"start": v(27.2, 44.1) * mm, "end": v(26.2, 44.1) * mm});
            skSolve(sketch);
        }
        {
            var Q0;
            {var subQ0=sQuery(id+"F22.wireOp",EDGE,"E55.top");Q0=makeQuery(id+"F22.imprint","IMPRINT",FACE,{"disambiguationData":[TD([[makeQuery(id+"F22.imprint","IMPRINT",EDGE,{"derivedFrom":subQ0}),-1.0]])]});}
            var Q1;
            {var subQ0=sQuery(id+"F22.wireOp",EDGE,"E55.bottom");Q1=makeQuery(id+"F22.imprint","IMPRINT",FACE,{"disambiguationData":[TD([[makeQuery(id+"F22.imprint","IMPRINT",EDGE,{"derivedFrom":subQ0}),1.0]])]});}
            var Q2;
            {var subQ4=sQuery(id+"F0.wireOp",EDGE,"E25.filletArc");var subQ6=sQuery(id+"F0.wireOp",EDGE,"E24.filletArc");var subQ8=sQuery(id+"F0.wireOp",EDGE,"E23.filletArc");var subQ10=sQuery(id+"F0.wireOp",EDGE,"E20.MirrorCS");var subQ12=sQuery(id+"F0.wireOp",EDGE,"E17.MirrorCS");var subQ14=sQuery(id+"F0.wireOp",EDGE,"E16.trimOffspring");var subQ16=sQuery(id+"F0.wireOp",EDGE,"E15.MirrorCS");var subQ18=sQuery(id+"F0.wireOp",EDGE,"E13.MirrorC");var subQ20=sQuery(id+"F0.wireOp",EDGE,"E12.MirrorCS");var subQ22=sQuery(id+"F0.wireOp",EDGE,"E9.filletArc");var subQ24=sQuery(id+"F0.wireOp",EDGE,"E19.MirrorCS");var subQ26=sQuery(id+"F0.wireOp",EDGE,"E8.filletArc");var subQ28=sQuery(id+"F0.wireOp",EDGE,"E18.MirrorC");var subQ30=sQuery(id+"F0.wireOp",EDGE,"E4");var subQ32=sQuery(id+"F0.wireOp",EDGE,"E1.1");var subQ33=sQuery(id+"F0.wireOp",EDGE,"E1.0");var subQ35=sQuery(id+"F0.wireOp",EDGE,"E14.MirrorCS");var subQ37=sQuery(id+"F0.wireOp",EDGE,"E3");var subQ40=sQuery(id+"F0.wireOp",EDGE,"E1.3");var subQ42=sQuery(id+"F0.wireOp",EDGE,"E1.2");var subQ45=sQuery(id+"F0.wireOp",EDGE,"E0.left");var subQ49=sQuery(id+"F0.wireOp",EDGE,"E0.top");var subQ53=makeQuery(id+"F1.opExtrude","SWEPT_FACE",FACE,{"disambiguationData":[OSD([subQ33])]});var subQ65=sQuery(id+"F0.wireOp",EDGE,"E21.trimOffspring");var subQ69=sQuery(id+"F0.wireOp",EDGE,"E7.trimOffspring");var subQ73=sQuery(id+"F0.wireOp",EDGE,"E0.bottom");var subQ75=sQuery(id+"F0.wireOp",EDGE,"E0.right");var subQ79=sQuery(id+"F0.wireOp",EDGE,"E11.filletArc");var subQ81=sQuery(id+"F0.wireOp",EDGE,"E10.filletArc");var subQ82=sQuery(id+"F0.wireOp",EDGE,"E5");var subQ83=sQuery(id+"F0.wireOp",EDGE,"E6.trimOffspring");var subQ84=sQuery(id+"F0.wireOp",EDGE,"E2");var subQ85=sQuery(id+"F0.wireOp",EDGE,"E22.filletArc");var subQ86=sQuery(id+"F4.wireOp",EDGE,"E29.right");var subQ87=sQuery(id+"F4.wireOp",EDGE,"E30");var subQ88=sQuery(id+"F4.wireOp",EDGE,"E31");var subQ89=sQuery(id+"F4.wireOp",EDGE,"E32.right");var subQ90=sQuery(id+"F4.wireOp",EDGE,"E34");Q2=makeQuery(id+"F19.boolean.opBoolean","MERGE",FACE,{"derivedFrom":[makeQuery(id+"F17.boolean.opBoolean","SPLIT",FACE,{"disambiguationData":[TD([subQ53])],"derivedFrom":makeQuery(id+"F14.boolean.opBoolean","SPLIT",FACE,{"disambiguationData":[TD([subQ53])],"derivedFrom":makeQuery(id+"F5.boolean.opBoolean","MERGE",FACE,{"derivedFrom":[makeQuery(id+"F2.opExtrude","CAP_FACE",FACE,{"disambiguationData":[OSD([subQ73,subQ49,subQ45,subQ75,subQ33,subQ32,subQ42,subQ40,subQ84,subQ37,subQ30,subQ82,subQ83,subQ69,subQ26,subQ22,subQ81,subQ79,subQ20,subQ18,subQ35,subQ16,subQ14,subQ12,subQ28,subQ24,subQ10,subQ65,subQ85,subQ8,subQ6,subQ4])],"isStart":false}),makeQuery(id+"F5.opExtrude","CAP_FACE",FACE,{"disambiguationData":[OSD([sQuery(id+"F4.wireOp",EDGE,"E29.left"),subQ86,subQ87,subQ88])],"isStart":true}),makeQuery(id+"F5.opExtrude","CAP_FACE",FACE,{"disambiguationData":[OSD([sQuery(id+"F4.wireOp",EDGE,"E32.left"),subQ89,sQuery(id+"F4.wireOp",EDGE,"E33"),subQ90])],"isStart":true})]})})}),makeQuery(id+"F19.opExtrude","CAP_FACE",FACE,{"disambiguationData":[OSD([sQuery(id+"F18.wireOp",EDGE,"E50.bottom"),sQuery(id+"F18.wireOp",EDGE,"E50.top"),sQuery(id+"F18.wireOp",EDGE,"E50.left"),sQuery(id+"F18.wireOp",EDGE,"E50.right")])],"isStart":true}),makeQuery(id+"F19.opExtrude","CAP_FACE",FACE,{"disambiguationData":[OSD([sQuery(id+"F18.wireOp",EDGE,"E51.bottom"),sQuery(id+"F18.wireOp",EDGE,"E51.top"),sQuery(id+"F18.wireOp",EDGE,"E51.left"),sQuery(id+"F18.wireOp",EDGE,"E51.right")])],"isStart":true})]});}
            extrude(context, id + "F23", {"entities" : qUnion([Q0, Q1]), "operationType" : NewBodyOperationType.REMOVE, "oppositeDirection" : true, "depth" : 0.8 * mm, "offsetDistance" : 25 * mm, "hasSecondDirection" : true, "secondDirectionBound" : SecondDirectionBoundingType.UP_TO_SURFACE, "secondDirectionOppositeDirection" : false, "secondDirectionDepth" : 25 * mm, "secondDirectionBoundEntityFace" : qUnion([Q2])});
        }
        {
            var Q0;
            {var subQ0=sQuery(id+"F22.wireOp",EDGE,"E56.top");Q0=makeQuery(id+"F22.imprint","IMPRINT",FACE,{"disambiguationData":[TD([[makeQuery(id+"F22.imprint","IMPRINT",EDGE,{"derivedFrom":subQ0}),-1.0]])]});}
            var Q1;
            {var subQ0=sQuery(id+"F22.wireOp",EDGE,"E57");Q1=makeQuery(id+"F22.imprint","IMPRINT",FACE,{"disambiguationData":[TD([[makeQuery(id+"F22.imprint","IMPRINT",EDGE,{"derivedFrom":subQ0}),1.0]])]});}
            var Q2;
            {var subQ0=sQuery(id+"F22.wireOp",EDGE,"E62.top");Q2=makeQuery(id+"F22.imprint","IMPRINT",FACE,{"disambiguationData":[TD([[makeQuery(id+"F22.imprint","IMPRINT",EDGE,{"derivedFrom":subQ0}),1.0]])]});}
            var Q3;
            Q3=makeQuery(id+"F22.imprint","IMPRINT",FACE,{"disambiguationData":[TD([[makeQuery(id+"F22.imprint","IMPRINT",EDGE,{"derivedFrom":sQuery(id+"F22.wireOp",EDGE,"E62.bottom")}),-1.0]])]});
            var Q4;
            Q4=makeQuery(id+"F1.opExtrude","CAP_FACE",FACE,{"disambiguationData":[OSD([sQuery(id+"F0.wireOp",EDGE,"E1.0"),sQuery(id+"F0.wireOp",EDGE,"E1.1"),sQuery(id+"F0.wireOp",EDGE,"E1.2"),sQuery(id+"F0.wireOp",EDGE,"E1.3"),sQuery(id+"F0.wireOp",EDGE,"E2"),sQuery(id+"F0.wireOp",EDGE,"E3"),sQuery(id+"F0.wireOp",EDGE,"E4"),sQuery(id+"F0.wireOp",EDGE,"E5"),sQuery(id+"F0.wireOp",EDGE,"E6.trimOffspring"),sQuery(id+"F0.wireOp",EDGE,"E7.trimOffspring"),sQuery(id+"F0.wireOp",EDGE,"E8.filletArc"),sQuery(id+"F0.wireOp",EDGE,"E9.filletArc"),sQuery(id+"F0.wireOp",EDGE,"E10.filletArc"),sQuery(id+"F0.wireOp",EDGE,"E11.filletArc"),sQuery(id+"F0.wireOp",EDGE,"E12.MirrorCS"),sQuery(id+"F0.wireOp",EDGE,"E13.MirrorC"),sQuery(id+"F0.wireOp",EDGE,"E14.MirrorCS"),sQuery(id+"F0.wireOp",EDGE,"E15.MirrorCS"),sQuery(id+"F0.wireOp",EDGE,"E16.trimOffspring"),sQuery(id+"F0.wireOp",EDGE,"E17.MirrorCS"),sQuery(id+"F0.wireOp",EDGE,"E18.MirrorC"),sQuery(id+"F0.wireOp",EDGE,"E19.MirrorCS"),sQuery(id+"F0.wireOp",EDGE,"E20.MirrorCS"),sQuery(id+"F0.wireOp",EDGE,"E21.trimOffspring")])],"isStart":false});
            var Q5;
            {var subQ0=sQuery(id+"F0.wireOp",EDGE,"E17.MirrorCS");var subQ2=sQuery(id+"F18.wireOp",EDGE,"E50.right");var subQ3=sQuery(id+"F0.wireOp",EDGE,"E16.trimOffspring");var subQ5=sQuery(id+"F18.wireOp",EDGE,"E50.left");var subQ6=sQuery(id+"F18.wireOp",EDGE,"E51.top");var subQ7=sQuery(id+"F0.wireOp",EDGE,"E14.MirrorCS");var subQ9=sQuery(id+"F0.wireOp",EDGE,"E1.0");var subQ10=makeQuery(id+"F1.opExtrude","SWEPT_FACE",FACE,{"disambiguationData":[OSD([subQ9])]});var subQ11=sQuery(id+"F0.wireOp",EDGE,"E13.MirrorC");var subQ13=sQuery(id+"F0.wireOp",EDGE,"E12.MirrorCS");var subQ16=sQuery(id+"F0.wireOp",EDGE,"E0.left");var subQ18=sQuery(id+"F0.wireOp",EDGE,"E0.top");var subQ20=sQuery(id+"F0.wireOp",EDGE,"E1.1");var subQ22=sQuery(id+"F0.wireOp",EDGE,"E15.MirrorCS");var subQ24=sQuery(id+"F18.wireOp",EDGE,"E50.top");var subQ25=sQuery(id+"F0.wireOp",EDGE,"E0.bottom");var subQ27=sQuery(id+"F0.wireOp",EDGE,"E20.MirrorCS");var subQ31=sQuery(id+"F0.wireOp",EDGE,"E1.3");var subQ33=sQuery(id+"F0.wireOp",EDGE,"E19.MirrorCS");var subQ35=sQuery(id+"F0.wireOp",EDGE,"E18.MirrorC");var subQ45=sQuery(id+"F0.wireOp",EDGE,"E23.filletArc");var subQ47=sQuery(id+"F18.wireOp",EDGE,"E51.right");var subQ48=sQuery(id+"F0.wireOp",EDGE,"E25.filletArc");var subQ50=sQuery(id+"F0.wireOp",EDGE,"E21.trimOffspring");var subQ59=sQuery(id+"F18.wireOp",EDGE,"E51.left");var subQ60=sQuery(id+"F0.wireOp",EDGE,"E24.filletArc");var subQ62=sQuery(id+"F0.wireOp",EDGE,"E9.filletArc");var subQ64=sQuery(id+"F0.wireOp",EDGE,"E8.filletArc");var subQ66=sQuery(id+"F0.wireOp",EDGE,"E4");var subQ68=sQuery(id+"F0.wireOp",EDGE,"E3");var subQ70=sQuery(id+"F0.wireOp",EDGE,"E1.2");var subQ81=sQuery(id+"F0.wireOp",EDGE,"E7.trimOffspring");var subQ84=sQuery(id+"F0.wireOp",EDGE,"E0.right");var subQ88=sQuery(id+"F0.wireOp",EDGE,"E11.filletArc");var subQ90=sQuery(id+"F0.wireOp",EDGE,"E10.filletArc");var subQ91=sQuery(id+"F0.wireOp",EDGE,"E5");var subQ92=sQuery(id+"F0.wireOp",EDGE,"E6.trimOffspring");var subQ93=sQuery(id+"F0.wireOp",EDGE,"E2");var subQ94=sQuery(id+"F0.wireOp",EDGE,"E22.filletArc");var subQ95=sQuery(id+"F4.wireOp",EDGE,"E29.right");var subQ96=sQuery(id+"F4.wireOp",EDGE,"E30");var subQ97=sQuery(id+"F4.wireOp",EDGE,"E31");var subQ98=sQuery(id+"F4.wireOp",EDGE,"E32.right");var subQ99=sQuery(id+"F4.wireOp",EDGE,"E34");Q5=makeQuery(id+"F23.boolean.opBoolean","SPLIT",FACE,{"disambiguationData":[TD([subQ10])],"derivedFrom":makeQuery(id+"F19.boolean.opBoolean","MERGE",FACE,{"derivedFrom":[makeQuery(id+"F17.boolean.opBoolean","SPLIT",FACE,{"disambiguationData":[TD([subQ10])],"derivedFrom":makeQuery(id+"F14.boolean.opBoolean","SPLIT",FACE,{"disambiguationData":[TD([subQ10])],"derivedFrom":makeQuery(id+"F5.boolean.opBoolean","MERGE",FACE,{"derivedFrom":[makeQuery(id+"F2.opExtrude","CAP_FACE",FACE,{"disambiguationData":[OSD([subQ25,subQ18,subQ16,subQ84,subQ9,subQ20,subQ70,subQ31,subQ93,subQ68,subQ66,subQ91,subQ92,subQ81,subQ64,subQ62,subQ90,subQ88,subQ13,subQ11,subQ7,subQ22,subQ3,subQ0,subQ35,subQ33,subQ27,subQ50,subQ94,subQ45,subQ60,subQ48])],"isStart":false}),makeQuery(id+"F5.opExtrude","CAP_FACE",FACE,{"disambiguationData":[OSD([sQuery(id+"F4.wireOp",EDGE,"E29.left"),subQ95,subQ96,subQ97])],"isStart":true}),makeQuery(id+"F5.opExtrude","CAP_FACE",FACE,{"disambiguationData":[OSD([sQuery(id+"F4.wireOp",EDGE,"E32.left"),subQ98,sQuery(id+"F4.wireOp",EDGE,"E33"),subQ99])],"isStart":true})]})})}),makeQuery(id+"F19.opExtrude","CAP_FACE",FACE,{"disambiguationData":[OSD([sQuery(id+"F18.wireOp",EDGE,"E50.bottom"),subQ24,subQ5,subQ2])],"isStart":true}),makeQuery(id+"F19.opExtrude","CAP_FACE",FACE,{"disambiguationData":[OSD([sQuery(id+"F18.wireOp",EDGE,"E51.bottom"),subQ6,subQ59,subQ47])],"isStart":true})]})});}
            extrude(context, id + "F24", {"entities" : qUnion([Q0, Q1, Q2, Q3]), "operationType" : NewBodyOperationType.REMOVE, "endBound" : BoundingType.UP_TO_SURFACE, "oppositeDirection" : true, "depth" : 25 * mm, "endBoundEntityFace" : qUnion([Q4]), "offsetDistance" : 25 * mm, "hasSecondDirection" : true, "secondDirectionBound" : SecondDirectionBoundingType.UP_TO_SURFACE, "secondDirectionOppositeDirection" : false, "secondDirectionDepth" : 25 * mm, "secondDirectionBoundEntityFace" : qUnion([Q5])});
        }
        {
            var Q0;
            Q0=makeQuery(id+"F1.opExtrude","CAP_FACE",FACE,{"disambiguationData":[OSD([sQuery(id+"F0.wireOp",EDGE,"E1.0"),sQuery(id+"F0.wireOp",EDGE,"E1.1"),sQuery(id+"F0.wireOp",EDGE,"E1.2"),sQuery(id+"F0.wireOp",EDGE,"E1.3"),sQuery(id+"F0.wireOp",EDGE,"E2"),sQuery(id+"F0.wireOp",EDGE,"E3"),sQuery(id+"F0.wireOp",EDGE,"E4"),sQuery(id+"F0.wireOp",EDGE,"E5"),sQuery(id+"F0.wireOp",EDGE,"E6.trimOffspring"),sQuery(id+"F0.wireOp",EDGE,"E7.trimOffspring"),sQuery(id+"F0.wireOp",EDGE,"E8.filletArc"),sQuery(id+"F0.wireOp",EDGE,"E9.filletArc"),sQuery(id+"F0.wireOp",EDGE,"E10.filletArc"),sQuery(id+"F0.wireOp",EDGE,"E11.filletArc"),sQuery(id+"F0.wireOp",EDGE,"E12.MirrorCS"),sQuery(id+"F0.wireOp",EDGE,"E13.MirrorC"),sQuery(id+"F0.wireOp",EDGE,"E14.MirrorCS"),sQuery(id+"F0.wireOp",EDGE,"E15.MirrorCS"),sQuery(id+"F0.wireOp",EDGE,"E16.trimOffspring"),sQuery(id+"F0.wireOp",EDGE,"E17.MirrorCS"),sQuery(id+"F0.wireOp",EDGE,"E18.MirrorC"),sQuery(id+"F0.wireOp",EDGE,"E19.MirrorCS"),sQuery(id+"F0.wireOp",EDGE,"E20.MirrorCS"),sQuery(id+"F0.wireOp",EDGE,"E21.trimOffspring")])],"isStart":true});
            var sketch = newSketch(context, id + "F25", { "sketchPlane" : qUnion([Q0])});
            skLineSegment(sketch, "E67.bottom", {"start": v(-25.5, 3.85) * mm, "end": v(-7.5, 3.85) * mm});
            skLineSegment(sketch, "E67.top", {"start": v(-25.5, 1.05) * mm, "end": v(-7.5, 1.05) * mm});
            skLineSegment(sketch, "E67.left", {"start": v(-25.5, 3.85) * mm, "end": v(-25.5, 1.05) * mm});
            skLineSegment(sketch, "E67.right", {"start": v(-7.5, 3.85) * mm, "end": v(-7.5, 1.05) * mm});
            skLineSegment(sketch, "E68.bottom", {"start": v(-9, -36.5) * mm, "end": v(9, -36.5) * mm});
            skLineSegment(sketch, "E68.top", {"start": v(-9, -39.3) * mm, "end": v(9, -39.3) * mm});
            skLineSegment(sketch, "E68.left", {"start": v(-9, -36.5) * mm, "end": v(-9, -39.3) * mm});
            skLineSegment(sketch, "E68.right", {"start": v(9, -36.5) * mm, "end": v(9, -39.3) * mm});
            skLineSegment(sketch, "E69.0", {"start": v(-25, 3.35) * mm, "end": v(-8, 3.35) * mm});
            skLineSegment(sketch, "E69.1", {"start": v(-25, 3.35) * mm, "end": v(-25, 1.55) * mm});
            skLineSegment(sketch, "E69.2", {"start": v(-25, 1.55) * mm, "end": v(-8, 1.55) * mm});
            skLineSegment(sketch, "E69.3", {"start": v(-8, 3.35) * mm, "end": v(-8, 1.55) * mm});
            skLineSegment(sketch, "E70", {"start": v(-25.5, 2.95) * mm, "end": v(-25, 2.95) * mm});
            skPoint(sketch, "E70.endSnap0", {"position": v(-25, 2.45) * mm});
            skLineSegment(sketch, "E71", {"start": v(-25.5, 1.95) * mm, "end": v(-25, 1.95) * mm});
            skLineSegment(sketch, "E72", {"start": v(-8, 2.95) * mm, "end": v(-7.5, 2.95) * mm});
            skLineSegment(sketch, "E73", {"start": v(-8, 1.95) * mm, "end": v(-7.5, 1.95) * mm});
            skLineSegment(sketch, "E74", {"start": v(-21.5, 3.85) * mm, "end": v(-21.5, 3.35) * mm});
            skLineSegment(sketch, "E75", {"start": v(-20.5, 3.85) * mm, "end": v(-20.5, 3.35) * mm});
            skLineSegment(sketch, "E76", {"start": v(-12.5, 3.85) * mm, "end": v(-12.5, 3.35) * mm});
            skLineSegment(sketch, "E77", {"start": v(-11.5, 3.85) * mm, "end": v(-11.5, 3.35) * mm});
            skLineSegment(sketch, "E78", {"start": v(-21.5, 1.55) * mm, "end": v(-21.5, 1.05) * mm});
            skLineSegment(sketch, "E79", {"start": v(-20.5, 1.55) * mm, "end": v(-20.5, 1.05) * mm});
            skLineSegment(sketch, "E80", {"start": v(-12.5, 1.55) * mm, "end": v(-12.5, 1.05) * mm});
            skLineSegment(sketch, "E81", {"start": v(-11.5, 1.55) * mm, "end": v(-11.5, 1.05) * mm});
            skLineSegment(sketch, "E82", {"start": v(-27.38, 2.45) * mm, "end": v(-5.26, 2.45) * mm, "construction": true});
            skLineSegment(sketch, "E83", {"start": v(-16.5, -0.43) * mm, "end": v(-16.5, 6.3) * mm, "construction": true});
            skPoint(sketch, "E83.startSnap0", {"position": v(-16.5, 1.05) * mm});
            skLineSegment(sketch, "E84.0", {"start": v(-8.5, -37) * mm, "end": v(8.5, -37) * mm});
            skLineSegment(sketch, "E84.1", {"start": v(-8.5, -37) * mm, "end": v(-8.5, -38.8) * mm});
            skLineSegment(sketch, "E84.2", {"start": v(-8.5, -38.8) * mm, "end": v(8.5, -38.8) * mm});
            skLineSegment(sketch, "E84.3", {"start": v(8.5, -37) * mm, "end": v(8.5, -38.8) * mm});
            skLineSegment(sketch, "E85", {"start": v(-11.15, -37.9) * mm, "end": v(10.75, -37.9) * mm, "construction": true});
            skPoint(sketch, "E85.startSnap0", {"position": v(-9, -37.9) * mm});
            skLineSegment(sketch, "E86", {"start": v(0, -35.08) * mm, "end": v(0, -40.45) * mm, "construction": true});
            skPoint(sketch, "E86.startSnap0", {"position": v(0, -36.5) * mm});
            skPoint(sketch, "E86.endSnap0", {"position": v(0, -39.3) * mm});
            skLineSegment(sketch, "E87", {"start": v(-5, -36.5) * mm, "end": v(-5, -37) * mm});
            skLineSegment(sketch, "E88", {"start": v(-4, -36.5) * mm, "end": v(-4, -37) * mm});
            skLineSegment(sketch, "E89", {"start": v(4, -36.5) * mm, "end": v(4, -37) * mm});
            skLineSegment(sketch, "E90", {"start": v(5, -36.5) * mm, "end": v(5, -37) * mm});
            skLineSegment(sketch, "E91", {"start": v(-9, -37.4) * mm, "end": v(-8.5, -37.4) * mm});
            skLineSegment(sketch, "E92", {"start": v(-9, -38.4) * mm, "end": v(-8.5, -38.4) * mm});
            skLineSegment(sketch, "E93", {"start": v(-5, -38.8) * mm, "end": v(-5, -39.3) * mm});
            skLineSegment(sketch, "E94", {"start": v(-4, -38.8) * mm, "end": v(-4, -39.3) * mm});
            skLineSegment(sketch, "E95", {"start": v(4, -38.8) * mm, "end": v(4, -39.3) * mm});
            skLineSegment(sketch, "E96", {"start": v(5, -38.8) * mm, "end": v(5, -39.3) * mm});
            skLineSegment(sketch, "E97", {"start": v(8.5, -37.4) * mm, "end": v(9, -37.4) * mm});
            skLineSegment(sketch, "E98", {"start": v(8.5, -38.4) * mm, "end": v(9, -38.4) * mm});
            skSolve(sketch);
        }
        {
            var Q0;
            {var subQ3=sQuery(id+"F25.wireOp",EDGE,"E70");Q0=makeQuery(id+"F25.imprint","IMPRINT",FACE,{"disambiguationData":[TD([[makeQuery(id+"F25.imprint","IMPRINT",EDGE,{"derivedFrom":subQ3}),1.0]])]});}
            var Q1;
            {var subQ3=sQuery(id+"F25.wireOp",EDGE,"E71");Q1=makeQuery(id+"F25.imprint","IMPRINT",FACE,{"disambiguationData":[TD([[makeQuery(id+"F25.imprint","IMPRINT",EDGE,{"derivedFrom":subQ3}),-1.0]])]});}
            var Q2;
            {var subQ0=sQuery(id+"F25.wireOp",EDGE,"E79");Q2=makeQuery(id+"F25.imprint","IMPRINT",FACE,{"disambiguationData":[TD([[makeQuery(id+"F25.imprint","IMPRINT",EDGE,{"derivedFrom":subQ0}),1.0]])]});}
            var Q3;
            {var subQ3=sQuery(id+"F25.wireOp",EDGE,"E73");Q3=makeQuery(id+"F25.imprint","IMPRINT",FACE,{"disambiguationData":[TD([[makeQuery(id+"F25.imprint","IMPRINT",EDGE,{"derivedFrom":subQ3}),-1.0]])]});}
            var Q4;
            {var subQ3=sQuery(id+"F25.wireOp",EDGE,"E72");Q4=makeQuery(id+"F25.imprint","IMPRINT",FACE,{"disambiguationData":[TD([[makeQuery(id+"F25.imprint","IMPRINT",EDGE,{"derivedFrom":subQ3}),1.0]])]});}
            var Q5;
            {var subQ0=sQuery(id+"F25.wireOp",EDGE,"E75");Q5=makeQuery(id+"F25.imprint","IMPRINT",FACE,{"disambiguationData":[TD([[makeQuery(id+"F25.imprint","IMPRINT",EDGE,{"derivedFrom":subQ0}),1.0]])]});}
            var Q6;
            {var subQ4=sQuery(id+"F25.wireOp",EDGE,"E87");Q6=makeQuery(id+"F25.imprint","IMPRINT",FACE,{"disambiguationData":[TD([[makeQuery(id+"F25.imprint","IMPRINT",EDGE,{"derivedFrom":subQ4}),-1.0]])]});}
            var Q7;
            {var subQ3=sQuery(id+"F25.wireOp",EDGE,"E92");Q7=makeQuery(id+"F25.imprint","IMPRINT",FACE,{"disambiguationData":[TD([[makeQuery(id+"F25.imprint","IMPRINT",EDGE,{"derivedFrom":subQ3}),-1.0]])]});}
            var Q8;
            {var subQ0=sQuery(id+"F25.wireOp",EDGE,"E94");Q8=makeQuery(id+"F25.imprint","IMPRINT",FACE,{"disambiguationData":[TD([[makeQuery(id+"F25.imprint","IMPRINT",EDGE,{"derivedFrom":subQ0}),1.0]])]});}
            var Q9;
            {var subQ3=sQuery(id+"F25.wireOp",EDGE,"E96");Q9=makeQuery(id+"F25.imprint","IMPRINT",FACE,{"disambiguationData":[TD([[makeQuery(id+"F25.imprint","IMPRINT",EDGE,{"derivedFrom":subQ3}),1.0]])]});}
            var Q10;
            {var subQ7=sQuery(id+"F25.wireOp",EDGE,"E90");Q10=makeQuery(id+"F25.imprint","IMPRINT",FACE,{"disambiguationData":[TD([[makeQuery(id+"F25.imprint","IMPRINT",EDGE,{"derivedFrom":subQ7}),1.0]])]});}
            var Q11;
            {var subQ0=sQuery(id+"F25.wireOp",EDGE,"E88");Q11=makeQuery(id+"F25.imprint","IMPRINT",FACE,{"disambiguationData":[TD([[makeQuery(id+"F25.imprint","IMPRINT",EDGE,{"derivedFrom":subQ0}),1.0]])]});}
            var Q12;
            Q12=makeQuery(id+"F1.opExtrude","CAP_FACE",FACE,{"disambiguationData":[OSD([sQuery(id+"F0.wireOp",EDGE,"E1.0"),sQuery(id+"F0.wireOp",EDGE,"E1.1"),sQuery(id+"F0.wireOp",EDGE,"E1.2"),sQuery(id+"F0.wireOp",EDGE,"E1.3"),sQuery(id+"F0.wireOp",EDGE,"E2"),sQuery(id+"F0.wireOp",EDGE,"E3"),sQuery(id+"F0.wireOp",EDGE,"E4"),sQuery(id+"F0.wireOp",EDGE,"E5"),sQuery(id+"F0.wireOp",EDGE,"E6.trimOffspring"),sQuery(id+"F0.wireOp",EDGE,"E7.trimOffspring"),sQuery(id+"F0.wireOp",EDGE,"E8.filletArc"),sQuery(id+"F0.wireOp",EDGE,"E9.filletArc"),sQuery(id+"F0.wireOp",EDGE,"E10.filletArc"),sQuery(id+"F0.wireOp",EDGE,"E11.filletArc"),sQuery(id+"F0.wireOp",EDGE,"E12.MirrorCS"),sQuery(id+"F0.wireOp",EDGE,"E13.MirrorC"),sQuery(id+"F0.wireOp",EDGE,"E14.MirrorCS"),sQuery(id+"F0.wireOp",EDGE,"E15.MirrorCS"),sQuery(id+"F0.wireOp",EDGE,"E16.trimOffspring"),sQuery(id+"F0.wireOp",EDGE,"E17.MirrorCS"),sQuery(id+"F0.wireOp",EDGE,"E18.MirrorC"),sQuery(id+"F0.wireOp",EDGE,"E19.MirrorCS"),sQuery(id+"F0.wireOp",EDGE,"E20.MirrorCS"),sQuery(id+"F0.wireOp",EDGE,"E21.trimOffspring")])],"isStart":false});
            extrude(context, id + "F26", {"entities" : qUnion([Q0, Q1, Q2, Q3, Q4, Q5, Q6, Q7, Q8, Q9, Q10, Q11]), "operationType" : NewBodyOperationType.REMOVE, "endBound" : BoundingType.UP_TO_SURFACE, "oppositeDirection" : true, "depth" : 25 * mm, "endBoundEntityFace" : qUnion([Q12]), "offsetDistance" : 25 * mm});
        }
        {
            var Q0;
            Q0=makeQuery(id+"F26.boolean.opBoolean","COPY",EDGE,{"derivedFrom":makeQuery(id+"F26.opExtrude","SWEPT_EDGE",EDGE,{"disambiguationData":[OSD([sQuery(id+"F25.wireOp",EDGE,"E67.bottom"),sQuery(id+"F25.wireOp",EDGE,"E67.left")])]})});
            var Q1;
            Q1=makeQuery(id+"F26.boolean.opBoolean","COPY",EDGE,{"derivedFrom":makeQuery(id+"F26.opExtrude","SWEPT_EDGE",EDGE,{"disambiguationData":[OSD([sQuery(id+"F25.wireOp",EDGE,"E67.top"),sQuery(id+"F25.wireOp",EDGE,"E67.left")])]})});
            var Q2;
            Q2=makeQuery(id+"F26.boolean.opBoolean","COPY",EDGE,{"derivedFrom":makeQuery(id+"F26.opExtrude","SWEPT_EDGE",EDGE,{"disambiguationData":[OSD([sQuery(id+"F25.wireOp",EDGE,"E67.top"),sQuery(id+"F25.wireOp",EDGE,"E67.right")])]})});
            var Q3;
            Q3=makeQuery(id+"F26.boolean.opBoolean","COPY",EDGE,{"derivedFrom":makeQuery(id+"F26.opExtrude","SWEPT_EDGE",EDGE,{"disambiguationData":[OSD([sQuery(id+"F25.wireOp",EDGE,"E67.bottom"),sQuery(id+"F25.wireOp",EDGE,"E67.right")])]})});
            var Q4;
            Q4=makeQuery(id+"F26.boolean.opBoolean","COPY",EDGE,{"derivedFrom":makeQuery(id+"F26.opExtrude","SWEPT_EDGE",EDGE,{"disambiguationData":[OSD([sQuery(id+"F25.wireOp",EDGE,"E68.top"),sQuery(id+"F25.wireOp",EDGE,"E68.left")])]})});
            var Q5;
            Q5=makeQuery(id+"F26.boolean.opBoolean","COPY",EDGE,{"derivedFrom":makeQuery(id+"F26.opExtrude","SWEPT_EDGE",EDGE,{"disambiguationData":[OSD([sQuery(id+"F25.wireOp",EDGE,"E68.bottom"),sQuery(id+"F25.wireOp",EDGE,"E68.left")])]})});
            var Q6;
            Q6=makeQuery(id+"F26.boolean.opBoolean","COPY",EDGE,{"derivedFrom":makeQuery(id+"F26.opExtrude","SWEPT_EDGE",EDGE,{"disambiguationData":[OSD([sQuery(id+"F25.wireOp",EDGE,"E68.bottom"),sQuery(id+"F25.wireOp",EDGE,"E68.right")])]})});
            var Q7;
            Q7=makeQuery(id+"F26.boolean.opBoolean","COPY",EDGE,{"derivedFrom":makeQuery(id+"F26.opExtrude","SWEPT_EDGE",EDGE,{"disambiguationData":[OSD([sQuery(id+"F25.wireOp",EDGE,"E68.top"),sQuery(id+"F25.wireOp",EDGE,"E68.right")])]})});
            fillet(context, id + "F27", {"entities" : qUnion([Q0, Q1, Q2, Q3, Q4, Q5, Q6, Q7]), "radius" : 0.5 * mm, "tangentPropagation" : true, "allowEdgeOverflow" : false});
        }
        {
            var Q0;
            Q0=makeQuery(id+"F1.opExtrude","CAP_FACE",FACE,{"disambiguationData":[OSD([sQuery(id+"F0.wireOp",EDGE,"E1.0"),sQuery(id+"F0.wireOp",EDGE,"E1.1"),sQuery(id+"F0.wireOp",EDGE,"E1.2"),sQuery(id+"F0.wireOp",EDGE,"E1.3"),sQuery(id+"F0.wireOp",EDGE,"E2"),sQuery(id+"F0.wireOp",EDGE,"E3"),sQuery(id+"F0.wireOp",EDGE,"E4"),sQuery(id+"F0.wireOp",EDGE,"E5"),sQuery(id+"F0.wireOp",EDGE,"E6.trimOffspring"),sQuery(id+"F0.wireOp",EDGE,"E7.trimOffspring"),sQuery(id+"F0.wireOp",EDGE,"E8.filletArc"),sQuery(id+"F0.wireOp",EDGE,"E9.filletArc"),sQuery(id+"F0.wireOp",EDGE,"E10.filletArc"),sQuery(id+"F0.wireOp",EDGE,"E11.filletArc"),sQuery(id+"F0.wireOp",EDGE,"E12.MirrorCS"),sQuery(id+"F0.wireOp",EDGE,"E13.MirrorC"),sQuery(id+"F0.wireOp",EDGE,"E14.MirrorCS"),sQuery(id+"F0.wireOp",EDGE,"E15.MirrorCS"),sQuery(id+"F0.wireOp",EDGE,"E16.trimOffspring"),sQuery(id+"F0.wireOp",EDGE,"E17.MirrorCS"),sQuery(id+"F0.wireOp",EDGE,"E18.MirrorC"),sQuery(id+"F0.wireOp",EDGE,"E19.MirrorCS"),sQuery(id+"F0.wireOp",EDGE,"E20.MirrorCS"),sQuery(id+"F0.wireOp",EDGE,"E21.trimOffspring")])],"isStart":true});
            var sketch = newSketch(context, id + "F28", { "sketchPlane" : qUnion([Q0])});
            skCircle(sketch, "E99", {"center": v(0, -17.4) * mm, "radius": 18.5 * mm});
            skCircle(sketch, "E100", {"center": v(-16.5, -0.9) * mm, "radius": 1.5 * mm});
            skCircle(sketch, "E101", {"center": v(15, -0.9) * mm, "radius": 1.5 * mm});
            skCircle(sketch, "E102", {"center": v(15, -33.9) * mm, "radius": 1.5 * mm});
            skCircle(sketch, "E103", {"center": v(-16.5, -33.9) * mm, "radius": 1.5 * mm});
            skSolve(sketch);
        }
        {
            var Q0;
            Q0 = qSketchRegion(id + "F28", true);
            var Q1;
            Q1=makeQuery(id+"F1.opExtrude","CAP_FACE",FACE,{"disambiguationData":[OSD([sQuery(id+"F0.wireOp",EDGE,"E1.0"),sQuery(id+"F0.wireOp",EDGE,"E1.1"),sQuery(id+"F0.wireOp",EDGE,"E1.2"),sQuery(id+"F0.wireOp",EDGE,"E1.3"),sQuery(id+"F0.wireOp",EDGE,"E2"),sQuery(id+"F0.wireOp",EDGE,"E3"),sQuery(id+"F0.wireOp",EDGE,"E4"),sQuery(id+"F0.wireOp",EDGE,"E5"),sQuery(id+"F0.wireOp",EDGE,"E6.trimOffspring"),sQuery(id+"F0.wireOp",EDGE,"E7.trimOffspring"),sQuery(id+"F0.wireOp",EDGE,"E8.filletArc"),sQuery(id+"F0.wireOp",EDGE,"E9.filletArc"),sQuery(id+"F0.wireOp",EDGE,"E10.filletArc"),sQuery(id+"F0.wireOp",EDGE,"E11.filletArc"),sQuery(id+"F0.wireOp",EDGE,"E12.MirrorCS"),sQuery(id+"F0.wireOp",EDGE,"E13.MirrorC"),sQuery(id+"F0.wireOp",EDGE,"E14.MirrorCS"),sQuery(id+"F0.wireOp",EDGE,"E15.MirrorCS"),sQuery(id+"F0.wireOp",EDGE,"E16.trimOffspring"),sQuery(id+"F0.wireOp",EDGE,"E17.MirrorCS"),sQuery(id+"F0.wireOp",EDGE,"E18.MirrorC"),sQuery(id+"F0.wireOp",EDGE,"E19.MirrorCS"),sQuery(id+"F0.wireOp",EDGE,"E20.MirrorCS"),sQuery(id+"F0.wireOp",EDGE,"E21.trimOffspring")])],"isStart":false});
            extrude(context, id + "F29", {"entities" : qUnion([Q0]), "operationType" : NewBodyOperationType.REMOVE, "endBound" : BoundingType.UP_TO_SURFACE, "oppositeDirection" : true, "depth" : 25 * mm, "endBoundEntityFace" : qUnion([Q1]), "offsetDistance" : 25 * mm});
        }
        {
            var Q0;
            Q0=makeQuery(id+"F28.imprint","IMPRINT",FACE,{"disambiguationData":[TD([[makeQuery(id+"F28.imprint","IMPRINT",EDGE,{"derivedFrom":sQuery(id+"F28.wireOp",EDGE,"E99")}),-1.0]])]});
            var sketch = newSketch(context, id + "F30", { "sketchPlane" : qUnion([Q0])});
            skLineSegment(sketch, "E104", {"start": v(24.5, 26.05) * mm, "end": v(24.5, -40.1) * mm, "construction": true});
            skLineSegment(sketch, "E105.bottom", {"start": v(26.5, 16) * mm, "end": v(22.5, 16) * mm});
            skLineSegment(sketch, "E105.top", {"start": v(26.5, -34.8) * mm, "end": v(22.5, -34.8) * mm});
            skLineSegment(sketch, "E105.left", {"start": v(26.5, 16) * mm, "end": v(26.5, -7.9) * mm});
            skLineSegment(sketch, "E105.right", {"start": v(22.5, 16) * mm, "end": v(22.5, -7.9) * mm});
            skPoint(sketch, "E105.middle", {"position": v(24.5, -9.4) * mm});
            skLineSegment(sketch, "E106.0", {"start": v(21.5, 17) * mm, "end": v(21.5, -8.9) * mm});
            skLineSegment(sketch, "E106.1", {"start": v(27.5, 17) * mm, "end": v(21.5, 17) * mm});
            skLineSegment(sketch, "E106.2", {"start": v(27.5, 17) * mm, "end": v(27.5, -8.9) * mm});
            skLineSegment(sketch, "E106.3", {"start": v(27.5, -35.8) * mm, "end": v(21.5, -35.8) * mm});
            skLineSegment(sketch, "E107", {"start": v(21.5, -8.9) * mm, "end": v(27.5, -8.9) * mm});
            skLineSegment(sketch, "E108", {"start": v(21.5, -9.9) * mm, "end": v(27.5, -9.9) * mm});
            skLineSegment(sketch, "E109.trimOffspring", {"start": v(21.5, -9.9) * mm, "end": v(21.5, -35.8) * mm});
            skLineSegment(sketch, "E110.trimOffspring", {"start": v(22.5, -10.9) * mm, "end": v(22.5, -34.8) * mm});
            skLineSegment(sketch, "E111.trimOffspring", {"start": v(26.5, -10.9) * mm, "end": v(26.5, -34.8) * mm});
            skLineSegment(sketch, "E112.trimOffspring", {"start": v(27.5, -9.9) * mm, "end": v(27.5, -35.8) * mm});
            skLineSegment(sketch, "E113.0", {"start": v(22.5, -7.9) * mm, "end": v(26.5, -7.9) * mm});
            skLineSegment(sketch, "E114.0", {"start": v(22.5, -10.9) * mm, "end": v(26.5, -10.9) * mm});
            skLineSegment(sketch, "E115", {"start": v(24, 17) * mm, "end": v(24, 16) * mm});
            skLineSegment(sketch, "E116", {"start": v(25, 17) * mm, "end": v(25, 16) * mm});
            skLineSegment(sketch, "E117", {"start": v(24, -7.9) * mm, "end": v(24, -8.9) * mm});
            skLineSegment(sketch, "E118", {"start": v(25, -7.9) * mm, "end": v(25, -8.9) * mm});
            skLineSegment(sketch, "E119", {"start": v(24, -9.9) * mm, "end": v(24, -10.9) * mm});
            skPoint(sketch, "E119.endSnap0", {"position": v(24.5, -10.9) * mm});
            skLineSegment(sketch, "E120", {"start": v(25, -9.9) * mm, "end": v(25, -10.9) * mm});
            skLineSegment(sketch, "E121", {"start": v(24, -34.8) * mm, "end": v(24, -35.8) * mm});
            skLineSegment(sketch, "E122", {"start": v(25, -34.8) * mm, "end": v(25, -35.8) * mm});
            skLineSegment(sketch, "E123", {"start": v(17.69, -22.85) * mm, "end": v(36.31, -22.85) * mm, "construction": true});
            skLineSegment(sketch, "E124", {"start": v(16.9, 4.05) * mm, "end": v(36.24, 4.05) * mm, "construction": true});
            skLineSegment(sketch, "E125", {"start": v(21.5, 10.78) * mm, "end": v(22.5, 10.78) * mm});
            skLineSegment(sketch, "E126", {"start": v(21.5, 9.78) * mm, "end": v(22.5, 9.78) * mm});
            skLineSegment(sketch, "E127", {"start": v(26.5, 10.78) * mm, "end": v(27.5, 10.78) * mm});
            skLineSegment(sketch, "E128", {"start": v(26.5, 9.78) * mm, "end": v(27.5, 9.78) * mm});
            skLineSegment(sketch, "E129", {"start": v(21.5, -1.67) * mm, "end": v(22.5, -1.67) * mm});
            skLineSegment(sketch, "E130", {"start": v(21.5, -2.67) * mm, "end": v(22.5, -2.67) * mm});
            skLineSegment(sketch, "E131", {"start": v(26.5, -1.67) * mm, "end": v(27.5, -1.67) * mm});
            skLineSegment(sketch, "E132", {"start": v(26.5, -2.67) * mm, "end": v(27.5, -2.67) * mm});
            skLineSegment(sketch, "E133", {"start": v(21.5, -16.12) * mm, "end": v(22.5, -16.12) * mm});
            skLineSegment(sketch, "E134", {"start": v(21.5, -17.12) * mm, "end": v(22.5, -17.12) * mm});
            skLineSegment(sketch, "E135", {"start": v(21.5, -28.57) * mm, "end": v(22.5, -28.57) * mm});
            skLineSegment(sketch, "E136", {"start": v(21.5, -29.57) * mm, "end": v(22.5, -29.57) * mm});
            skLineSegment(sketch, "E137", {"start": v(26.5, -16.12) * mm, "end": v(27.5, -16.12) * mm});
            skLineSegment(sketch, "E138", {"start": v(26.5, -17.12) * mm, "end": v(27.5, -17.12) * mm});
            skLineSegment(sketch, "E139", {"start": v(26.5, -28.57) * mm, "end": v(27.5, -28.57) * mm});
            skLineSegment(sketch, "E140", {"start": v(26.5, -29.57) * mm, "end": v(27.5, -29.57) * mm});
            skSolve(sketch);
        }
        {
            var Q0;
            {var subQ3=sQuery(id+"F30.wireOp",EDGE,"E115");Q0=makeQuery(id+"F30.imprint","IMPRINT",FACE,{"disambiguationData":[TD([[makeQuery(id+"F30.imprint","IMPRINT",EDGE,{"derivedFrom":subQ3}),-1.0]])]});}
            var Q1;
            {var subQ4=sQuery(id+"F30.wireOp",EDGE,"E116");Q1=makeQuery(id+"F30.imprint","IMPRINT",FACE,{"disambiguationData":[TD([[makeQuery(id+"F30.imprint","IMPRINT",EDGE,{"derivedFrom":subQ4}),1.0]])]});}
            var Q2;
            {var subQ0=sQuery(id+"F30.wireOp",EDGE,"E126");Q2=makeQuery(id+"F30.imprint","IMPRINT",FACE,{"disambiguationData":[TD([[makeQuery(id+"F30.imprint","IMPRINT",EDGE,{"derivedFrom":subQ0}),-1.0]])]});}
            var Q3;
            {var subQ0=sQuery(id+"F30.wireOp",EDGE,"E128");Q3=makeQuery(id+"F30.imprint","IMPRINT",FACE,{"disambiguationData":[TD([[makeQuery(id+"F30.imprint","IMPRINT",EDGE,{"derivedFrom":subQ0}),-1.0]])]});}
            var Q4;
            {var subQ3=sQuery(id+"F30.wireOp",EDGE,"E117");Q4=makeQuery(id+"F30.imprint","IMPRINT",FACE,{"disambiguationData":[TD([[makeQuery(id+"F30.imprint","IMPRINT",EDGE,{"derivedFrom":subQ3}),-1.0]])]});}
            var Q5;
            {var subQ3=sQuery(id+"F30.wireOp",EDGE,"E118");Q5=makeQuery(id+"F30.imprint","IMPRINT",FACE,{"disambiguationData":[TD([[makeQuery(id+"F30.imprint","IMPRINT",EDGE,{"derivedFrom":subQ3}),1.0]])]});}
            var Q6;
            {var subQ3=sQuery(id+"F30.wireOp",EDGE,"E119");Q6=makeQuery(id+"F30.imprint","IMPRINT",FACE,{"disambiguationData":[TD([[makeQuery(id+"F30.imprint","IMPRINT",EDGE,{"derivedFrom":subQ3}),-1.0]])]});}
            var Q7;
            {var subQ3=sQuery(id+"F30.wireOp",EDGE,"E120");Q7=makeQuery(id+"F30.imprint","IMPRINT",FACE,{"disambiguationData":[TD([[makeQuery(id+"F30.imprint","IMPRINT",EDGE,{"derivedFrom":subQ3}),1.0]])]});}
            var Q8;
            {var subQ0=sQuery(id+"F30.wireOp",EDGE,"E134");Q8=makeQuery(id+"F30.imprint","IMPRINT",FACE,{"disambiguationData":[TD([[makeQuery(id+"F30.imprint","IMPRINT",EDGE,{"derivedFrom":subQ0}),-1.0]])]});}
            var Q9;
            {var subQ0=sQuery(id+"F30.wireOp",EDGE,"E138");Q9=makeQuery(id+"F30.imprint","IMPRINT",FACE,{"disambiguationData":[TD([[makeQuery(id+"F30.imprint","IMPRINT",EDGE,{"derivedFrom":subQ0}),-1.0]])]});}
            var Q10;
            {var subQ7=sQuery(id+"F30.wireOp",EDGE,"E121");Q10=makeQuery(id+"F30.imprint","IMPRINT",FACE,{"disambiguationData":[TD([[makeQuery(id+"F30.imprint","IMPRINT",EDGE,{"derivedFrom":subQ7}),-1.0]])]});}
            var Q11;
            {var subQ7=sQuery(id+"F30.wireOp",EDGE,"E122");Q11=makeQuery(id+"F30.imprint","IMPRINT",FACE,{"disambiguationData":[TD([[makeQuery(id+"F30.imprint","IMPRINT",EDGE,{"derivedFrom":subQ7}),1.0]])]});}
            var Q12;
            Q12=makeQuery(id+"F1.opExtrude","CAP_FACE",FACE,{"disambiguationData":[OSD([sQuery(id+"F0.wireOp",EDGE,"E1.0"),sQuery(id+"F0.wireOp",EDGE,"E1.1"),sQuery(id+"F0.wireOp",EDGE,"E1.2"),sQuery(id+"F0.wireOp",EDGE,"E1.3"),sQuery(id+"F0.wireOp",EDGE,"E2"),sQuery(id+"F0.wireOp",EDGE,"E3"),sQuery(id+"F0.wireOp",EDGE,"E4"),sQuery(id+"F0.wireOp",EDGE,"E5"),sQuery(id+"F0.wireOp",EDGE,"E6.trimOffspring"),sQuery(id+"F0.wireOp",EDGE,"E7.trimOffspring"),sQuery(id+"F0.wireOp",EDGE,"E8.filletArc"),sQuery(id+"F0.wireOp",EDGE,"E9.filletArc"),sQuery(id+"F0.wireOp",EDGE,"E10.filletArc"),sQuery(id+"F0.wireOp",EDGE,"E11.filletArc"),sQuery(id+"F0.wireOp",EDGE,"E12.MirrorCS"),sQuery(id+"F0.wireOp",EDGE,"E13.MirrorC"),sQuery(id+"F0.wireOp",EDGE,"E14.MirrorCS"),sQuery(id+"F0.wireOp",EDGE,"E15.MirrorCS"),sQuery(id+"F0.wireOp",EDGE,"E16.trimOffspring"),sQuery(id+"F0.wireOp",EDGE,"E17.MirrorCS"),sQuery(id+"F0.wireOp",EDGE,"E18.MirrorC"),sQuery(id+"F0.wireOp",EDGE,"E19.MirrorCS"),sQuery(id+"F0.wireOp",EDGE,"E20.MirrorCS"),sQuery(id+"F0.wireOp",EDGE,"E21.trimOffspring")])],"isStart":false});
            extrude(context, id + "F31", {"entities" : qUnion([Q0, Q1, Q2, Q3, Q4, Q5, Q6, Q7, Q8, Q9, Q10, Q11]), "operationType" : NewBodyOperationType.REMOVE, "endBound" : BoundingType.UP_TO_SURFACE, "oppositeDirection" : true, "depth" : 25 * mm, "endBoundEntityFace" : qUnion([Q12]), "offsetDistance" : 25 * mm});
        }
    });
